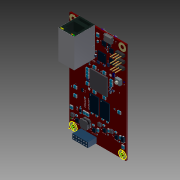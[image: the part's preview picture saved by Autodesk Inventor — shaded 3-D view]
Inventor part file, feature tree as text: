
AUTODESK INVENTOR PART (.ipt)
format: ipt  version: 2015 (Build 190159000, 159)  size: 6,993,920 bytes
history: native  units: in
note: dims shown in document units (in); Inventor stores cm internally (conversion verified against a paired STEP export)
features: imported_body x1163, extrude x1112, other x52, projected_geometry x25, sketch x3
ambient origin geometry x8: Origin, YZ Plane, XZ Plane, XY Plane, X Axis, Y Axis, Z Axis, Center Point
bodies: Body1 (feature_tree), Body2 (feature_tree), Body3 (feature_tree), Body4 (feature_tree), Body5 (feature_tree), Body6 (feature_tree), Body7 (feature_tree), Body8 (feature_tree), Body9 (feature_tree), Body10 (feature_tree), Body11 (feature_tree), Body12 (feature_tree), Body13 (feature_tree), Body14 (feature_tree), Body15 (feature_tree), Body16 (feature_tree), Body17 (feature_tree), Body18 (feature_tree), Body19 (feature_tree), Body20 (feature_tree), Body21 (feature_tree), Body22 (feature_tree), Body23 (feature_tree), Body24 (feature_tree), Body25 (feature_tree), Body26 (feature_tree), Body27 (feature_tree), Body28 (feature_tree), Body29 (feature_tree), Body30 (feature_tree), Body31 (feature_tree), Body32 (feature_tree), Body33 (feature_tree), Body34 (feature_tree), Body35 (feature_tree), Body36 (feature_tree), Body37 (feature_tree), Body38 (feature_tree), Body39 (feature_tree), Body40 (feature_tree), Body41 (feature_tree), Body42 (feature_tree), Body43 (feature_tree), Body44 (feature_tree), Body45 (feature_tree), Body46 (feature_tree), Body47 (feature_tree), Body48 (feature_tree), Body49 (feature_tree), Body50 (feature_tree), Body51 (feature_tree), Body52 (feature_tree), Body53 (feature_tree), Body54 (feature_tree), Body55 (feature_tree), Body56 (feature_tree), Body57 (feature_tree), Body58 (feature_tree), Body59 (feature_tree), Body60 (feature_tree), Body61 (feature_tree), Body62 (feature_tree), Body63 (feature_tree), Body64 (feature_tree), Body65 (feature_tree), Body66 (feature_tree), Body67 (feature_tree), Body68 (feature_tree), Body69 (feature_tree), Body70 (feature_tree), Body71 (feature_tree), Body72 (feature_tree), Body73 (feature_tree), Body74 (feature_tree), Body75 (feature_tree), Body76 (feature_tree), Body77 (feature_tree), Body78 (feature_tree), Body79 (feature_tree), Body80 (feature_tree), Body81 (feature_tree), Body82 (feature_tree), Body83 (feature_tree), Body84 (feature_tree), Body85 (feature_tree), Body86 (feature_tree), Body87 (feature_tree), Body88 (feature_tree), Body89 (feature_tree), Body90 (feature_tree), Body91 (feature_tree), Body92 (feature_tree), Body93 (feature_tree), Body94 (feature_tree), Body95 (feature_tree), Body96 (feature_tree), Body97 (feature_tree), Body98 (feature_tree), Body99 (feature_tree), Body100 (feature_tree), Body101 (feature_tree), Body102 (feature_tree), Body103 (feature_tree), Body104 (feature_tree), Body105 (feature_tree), Body106 (feature_tree), Body107 (feature_tree), Body108 (feature_tree), Body109 (feature_tree), Body110 (feature_tree), Body111 (feature_tree), Body112 (feature_tree), Body113 (feature_tree), Body114 (feature_tree), Body115 (feature_tree), Body116 (feature_tree), Body117 (feature_tree), Body118 (feature_tree), Body119 (feature_tree), Body120 (feature_tree), Body121 (feature_tree), Body122 (feature_tree), Body123 (feature_tree), Body124 (feature_tree), Body125 (feature_tree), Body126 (feature_tree), Body127 (feature_tree), Body128 (feature_tree), Body129 (feature_tree), Body130 (feature_tree), Body131 (feature_tree), Body132 (feature_tree), Body133 (feature_tree), Body134 (feature_tree), Body135 (feature_tree), Body136 (feature_tree), Body137 (feature_tree), Body138 (feature_tree), Body139 (feature_tree), Body140 (feature_tree), Body141 (feature_tree), Body142 (feature_tree), Body143 (feature_tree), Body144 (feature_tree), Body145 (feature_tree), Body146 (feature_tree), Body147 (feature_tree), Body148 (feature_tree), Body149 (feature_tree), Body150 (feature_tree), Body151 (feature_tree), Body152 (feature_tree), Body153 (feature_tree), Body154 (feature_tree), Body155 (feature_tree), Body156 (feature_tree), Body157 (feature_tree), Body158 (feature_tree), Body159 (feature_tree), Body160 (feature_tree), Body161 (feature_tree), Body162 (feature_tree), Body163 (feature_tree), Body164 (feature_tree), Body165 (feature_tree), Body166 (feature_tree), Body167 (feature_tree), Body168 (feature_tree), Body169 (feature_tree), Body170 (feature_tree), Body171 (feature_tree), Body172 (feature_tree), Body173 (feature_tree), Body174 (feature_tree), Body175 (feature_tree), Body176 (feature_tree), Body177 (feature_tree), Body178 (feature_tree), Body179 (feature_tree), Body180 (feature_tree), Body181 (feature_tree), Body182 (feature_tree), Body183 (feature_tree), Body184 (feature_tree), Body185 (feature_tree), Body186 (feature_tree), Body187 (feature_tree), Body188 (feature_tree), Body189 (feature_tree), Body190 (feature_tree), Body191 (feature_tree), Body192 (feature_tree), Body193 (feature_tree), Body194 (feature_tree), Body195 (feature_tree), Body196 (feature_tree), Body197 (feature_tree), Body198 (feature_tree), Body199 (feature_tree), Body200 (feature_tree), Body201 (feature_tree), Body202 (feature_tree), Body203 (feature_tree), Body204 (feature_tree), Body205 (feature_tree), Body206 (feature_tree), Body207 (feature_tree), Body208 (feature_tree), Body209 (feature_tree), Body210 (feature_tree), Body211 (feature_tree), Body212 (feature_tree), Body213 (feature_tree), Body214 (feature_tree), Body215 (feature_tree), Body216 (feature_tree), Body217 (feature_tree), Body218 (feature_tree), Body219 (feature_tree), Body220 (feature_tree), Body221 (feature_tree), Body222 (feature_tree), Body223 (feature_tree), Body224 (feature_tree), Body225 (feature_tree), Body226 (feature_tree), Body227 (feature_tree), Body228 (feature_tree), Body229 (feature_tree), Body230 (feature_tree), Body231 (feature_tree), Body232 (feature_tree), Body233 (feature_tree), Body234 (feature_tree), Body235 (feature_tree), Body236 (feature_tree), Body237 (feature_tree), Body238 (feature_tree), Body239 (feature_tree), Body240 (feature_tree), Body241 (feature_tree), Body242 (feature_tree), Body243 (feature_tree), Body244 (feature_tree), Body245 (feature_tree), Body246 (feature_tree), Body247 (feature_tree), Body248 (feature_tree), Body249 (feature_tree), Body250 (feature_tree), Body251 (feature_tree), Body252 (feature_tree), Body253 (feature_tree), Body254 (feature_tree), Body255 (feature_tree), Body256 (feature_tree), Body257 (feature_tree), Body258 (feature_tree), Body259 (feature_tree), Body260 (feature_tree), Body261 (feature_tree), Body262 (feature_tree), Body263 (feature_tree), Body264 (feature_tree), Body265 (feature_tree), Body266 (feature_tree), Body267 (feature_tree), Body268 (feature_tree), Body269 (feature_tree), Body270 (feature_tree), Body271 (feature_tree), Body272 (feature_tree), Body273 (feature_tree), Body274 (feature_tree), Body275 (feature_tree), Body276 (feature_tree), Body277 (feature_tree), Body278 (feature_tree), Body279 (feature_tree), Body280 (feature_tree), Body281 (feature_tree), Body282 (feature_tree), Body283 (feature_tree), Body284 (feature_tree), Body285 (feature_tree), Body286 (feature_tree), Body287 (feature_tree), Body288 (feature_tree), Body289 (feature_tree), Body290 (feature_tree), Body291 (feature_tree), Body292 (feature_tree), Body293 (feature_tree), Body294 (feature_tree), Body295 (feature_tree), Body296 (feature_tree), Body297 (feature_tree), Body298 (feature_tree), Body299 (feature_tree), Body300 (feature_tree), Body301 (feature_tree), Body302 (feature_tree), Body303 (feature_tree), Body304 (feature_tree), Body305 (feature_tree), Body306 (feature_tree), Body307 (feature_tree), Body308 (feature_tree), Body309 (feature_tree), Body310 (feature_tree), Body311 (feature_tree), Body312 (feature_tree), Body313 (feature_tree), Body314 (feature_tree), Body315 (feature_tree), Body316 (feature_tree), Body317 (feature_tree), Body318 (feature_tree), Body319 (feature_tree), Body320 (feature_tree), Body321 (feature_tree), Body322 (feature_tree), Body323 (feature_tree), Body324 (feature_tree), Body325 (feature_tree), Body326 (feature_tree), Body327 (feature_tree), Body328 (feature_tree), Body329 (feature_tree), Body330 (feature_tree), Body331 (feature_tree), Body332 (feature_tree), Body333 (feature_tree), Body334 (feature_tree), Body335 (feature_tree), Body336 (feature_tree), Body337 (feature_tree), Body338 (feature_tree), Body339 (feature_tree), Body340 (feature_tree), Body341 (feature_tree), Body342 (feature_tree), Body343 (feature_tree), Body344 (feature_tree), Body345 (feature_tree), Body346 (feature_tree), Body347 (feature_tree), Body348 (feature_tree), Body349 (feature_tree), Body350 (feature_tree), Body351 (feature_tree), Body352 (feature_tree), Body353 (feature_tree), Body354 (feature_tree), Body355 (feature_tree), Body356 (feature_tree), Body357 (feature_tree), Body358 (feature_tree), Body359 (feature_tree), Body360 (feature_tree), Body361 (feature_tree), Body362 (feature_tree), Body363 (feature_tree), Body364 (feature_tree), Body365 (feature_tree), Body366 (feature_tree), Body367 (feature_tree), Body368 (feature_tree), Body369 (feature_tree), Body370 (feature_tree), Body371 (feature_tree), Body372 (feature_tree), Body373 (feature_tree), Body374 (feature_tree), Body375 (feature_tree), Body376 (feature_tree), Body377 (feature_tree), Body378 (feature_tree), Body379 (feature_tree), Body380 (feature_tree), Body381 (feature_tree), Body382 (feature_tree), Body383 (feature_tree), Body384 (feature_tree), Body385 (feature_tree), Body386 (feature_tree), Body387 (feature_tree), Body388 (feature_tree), Body389 (feature_tree), Body390 (feature_tree), Body391 (feature_tree), Body392 (feature_tree), Body393 (feature_tree), Body394 (feature_tree), Body395 (feature_tree), Body396 (feature_tree), Body397 (feature_tree), Body398 (feature_tree), Body399 (feature_tree), Body400 (feature_tree), Body401 (feature_tree), Body402 (feature_tree), Body403 (feature_tree), Body404 (feature_tree), Body405 (feature_tree), Body406 (feature_tree), Body407 (feature_tree), Body408 (feature_tree), Body409 (feature_tree), Body410 (feature_tree), Body411 (feature_tree), Body412 (feature_tree), Body413 (feature_tree), Body414 (feature_tree), Body415 (feature_tree), Body416 (feature_tree), Body417 (feature_tree), Body418 (feature_tree), Body419 (feature_tree), Body420 (feature_tree), Body421 (feature_tree), Body422 (feature_tree), Body423 (feature_tree), Body424 (feature_tree), Body425 (feature_tree), Body426 (feature_tree), Body427 (feature_tree), Body428 (feature_tree), Body429 (feature_tree), Body430 (feature_tree), Body431 (feature_tree), Body432 (feature_tree), Body433 (feature_tree), Body434 (feature_tree), Body435 (feature_tree), Body436 (feature_tree), Body437 (feature_tree), Body438 (feature_tree), Body439 (feature_tree), Body440 (feature_tree), Body441 (feature_tree), Body442 (feature_tree), Body443 (feature_tree), Body444 (feature_tree), Body445 (feature_tree), Body446 (feature_tree), Body447 (feature_tree), Body448 (feature_tree), Body449 (feature_tree), Body450 (feature_tree), Body451 (feature_tree), Body452 (feature_tree), Body453 (feature_tree), Body454 (feature_tree), Body455 (feature_tree), Body456 (feature_tree), Body457 (feature_tree), Body458 (feature_tree), Body459 (feature_tree), Body460 (feature_tree), Body461 (feature_tree), Body462 (feature_tree), Body463 (feature_tree), Body464 (feature_tree), Body465 (feature_tree), Body466 (feature_tree), Body467 (feature_tree), Body468 (feature_tree), Body469 (feature_tree), Body470 (feature_tree), Body471 (feature_tree), Body472 (feature_tree), Body473 (feature_tree), Body474 (feature_tree), Body475 (feature_tree), Body476 (feature_tree), Body477 (feature_tree), Body478 (feature_tree), Body479 (feature_tree), Body480 (feature_tree), Body481 (feature_tree), Body482 (feature_tree), Body483 (feature_tree), Body484 (feature_tree), Body485 (feature_tree), Body486 (feature_tree), Body487 (feature_tree), Body488 (feature_tree), Body489 (feature_tree), Body490 (feature_tree), Body491 (feature_tree), Body492 (feature_tree), Body493 (feature_tree), Body494 (feature_tree), Body495 (feature_tree), Body496 (feature_tree), Body497 (feature_tree), Body498 (feature_tree), Body499 (feature_tree), Body500 (feature_tree), Body501 (feature_tree), Body502 (feature_tree), Body503 (feature_tree), Body504 (feature_tree), Body505 (feature_tree), Body506 (feature_tree), Body507 (feature_tree), Body508 (feature_tree), Body509 (feature_tree), Body510 (feature_tree), Body511 (feature_tree), Body512 (feature_tree), Body513 (feature_tree), Body514 (feature_tree), Body515 (feature_tree), Body516 (feature_tree), Body517 (feature_tree), Body518 (feature_tree), Body519 (feature_tree), Body520 (feature_tree), Body521 (feature_tree), Body522 (feature_tree), Body523 (feature_tree), Body524 (feature_tree), Body525 (feature_tree), Body526 (feature_tree), Body527 (feature_tree), Body528 (feature_tree), Body529 (feature_tree), Body530 (feature_tree), Body531 (feature_tree), Body532 (feature_tree), Body533 (feature_tree), Body534 (feature_tree), Body535 (feature_tree), Body536 (feature_tree), Body537 (feature_tree), Body538 (feature_tree), Body539 (feature_tree), Body540 (feature_tree), Body541 (feature_tree), Body542 (feature_tree), Body543 (feature_tree), Body544 (feature_tree), Body545 (feature_tree), Body546 (feature_tree), Body547 (feature_tree), Body548 (feature_tree), Body549 (feature_tree), Body550 (feature_tree), Body551 (feature_tree), Body552 (feature_tree), Body553 (feature_tree), Body554 (feature_tree), Body555 (feature_tree), Body556 (feature_tree), Body557 (feature_tree), Body558 (feature_tree), Body559 (feature_tree), Body560 (feature_tree), Body561 (feature_tree), Body562 (feature_tree), Body563 (feature_tree), Body564 (feature_tree), Body565 (feature_tree), Body566 (feature_tree), Body567 (feature_tree), Body568 (feature_tree), Body569 (feature_tree), Body570 (feature_tree), Body571 (feature_tree), Body572 (feature_tree), Body573 (feature_tree), Body574 (feature_tree), Body575 (feature_tree), Body576 (feature_tree), Body577 (feature_tree), Body578 (feature_tree), Body579 (feature_tree), Body580 (feature_tree), Body581 (feature_tree), Body582 (feature_tree), Body583 (feature_tree), Body584 (feature_tree), Body585 (feature_tree), Body586 (feature_tree), Body587 (feature_tree), Body588 (feature_tree), Body589 (feature_tree), Body590 (feature_tree), Body591 (feature_tree), Body592 (feature_tree), Body593 (feature_tree), Body594 (feature_tree), Body595 (feature_tree), Body596 (feature_tree), Body597 (feature_tree), Body598 (feature_tree), Body599 (feature_tree), Body600 (feature_tree), Body601 (feature_tree), Body602 (feature_tree), Body603 (feature_tree), Body604 (feature_tree), Body605 (feature_tree), Body606 (feature_tree), Body607 (feature_tree), Body608 (feature_tree), Body609 (feature_tree), Body610 (feature_tree), Body611 (feature_tree), Body612 (feature_tree), Body613 (feature_tree), Body614 (feature_tree), Body615 (feature_tree), Body616 (feature_tree), Body617 (feature_tree), Body618 (feature_tree), Body619 (feature_tree), Body620 (feature_tree), Body621 (feature_tree), Body622 (feature_tree), Body623 (feature_tree), Body624 (feature_tree), Body625 (feature_tree), Body626 (feature_tree), Body627 (feature_tree), Body628 (feature_tree), Body629 (feature_tree), Body630 (feature_tree), Body631 (feature_tree), Body632 (feature_tree), Body633 (feature_tree), Body634 (feature_tree), Body635 (feature_tree), Body636 (feature_tree), Body637 (feature_tree), Body638 (feature_tree), Body639 (feature_tree), Body640 (feature_tree), Body641 (feature_tree), Body642 (feature_tree), Body643 (feature_tree), Body644 (feature_tree), Body645 (feature_tree), Body646 (feature_tree), Body647 (feature_tree), Body648 (feature_tree), Body649 (feature_tree), Body650 (feature_tree), Body651 (feature_tree), Body652 (feature_tree), Body653 (feature_tree), Body654 (feature_tree), Body655 (feature_tree), Body656 (feature_tree), Body657 (feature_tree), Body658 (feature_tree), Body659 (feature_tree), Body660 (feature_tree), Body661 (feature_tree), Body662 (feature_tree), Body663 (feature_tree), Body664 (feature_tree), Body665 (feature_tree), Body666 (feature_tree), Body667 (feature_tree), Body668 (feature_tree), Body669 (feature_tree), Body670 (feature_tree), Body671 (feature_tree), Body672 (feature_tree), Body673 (feature_tree), Body674 (feature_tree), Body675 (feature_tree), Body676 (feature_tree), Body677 (feature_tree), Body678 (feature_tree), Body679 (feature_tree), Body680 (feature_tree), Body681 (feature_tree), Body682 (feature_tree), Body683 (feature_tree), Body684 (feature_tree), Body685 (feature_tree), Body686 (feature_tree), Body687 (feature_tree), Body688 (feature_tree), Body689 (feature_tree), Body690 (feature_tree), Body691 (feature_tree), Body692 (feature_tree), Body693 (feature_tree), Body694 (feature_tree), Body695 (feature_tree), Body696 (feature_tree), Body697 (feature_tree), Body698 (feature_tree), Body699 (feature_tree), Body700 (feature_tree), Body701 (feature_tree), Body702 (feature_tree), Body703 (feature_tree), Body704 (feature_tree), Body705 (feature_tree), Body706 (feature_tree), Body707 (feature_tree), Body708 (feature_tree), Body709 (feature_tree), Body710 (feature_tree), Body711 (feature_tree), Body712 (feature_tree), Body713 (feature_tree), Body714 (feature_tree), Body715 (feature_tree), Body716 (feature_tree), Body717 (feature_tree), Body718 (feature_tree), Body719 (feature_tree), Body720 (feature_tree), Body721 (feature_tree), Body722 (feature_tree), Body723 (feature_tree), Body724 (feature_tree), Body725 (feature_tree), Body726 (feature_tree), Body727 (feature_tree), Body728 (feature_tree), Body729 (feature_tree), Body730 (feature_tree), Body731 (feature_tree), Body732 (feature_tree), Body733 (feature_tree), Body734 (feature_tree), Body735 (feature_tree), Body736 (feature_tree), Body737 (feature_tree), Body738 (feature_tree), Body739 (feature_tree), Body740 (feature_tree), Body741 (feature_tree), Body742 (feature_tree), Body743 (feature_tree), Body744 (feature_tree), Body745 (feature_tree), Body746 (feature_tree), Body747 (feature_tree), Body748 (feature_tree), Body749 (feature_tree), Body750 (feature_tree), Body751 (feature_tree), Body752 (feature_tree), Body753 (feature_tree), Body754 (feature_tree), Body755 (feature_tree), Body756 (feature_tree), Body757 (feature_tree), Body758 (feature_tree), Body759 (feature_tree), Body760 (feature_tree), Body761 (feature_tree), Body762 (feature_tree), Body763 (feature_tree), Body764 (feature_tree), Body765 (feature_tree), Body766 (feature_tree), Body767 (feature_tree), Body768 (feature_tree), Body769 (feature_tree), Body770 (feature_tree), Body771 (feature_tree), Body772 (feature_tree), Body773 (feature_tree), Body774 (feature_tree), Body775 (feature_tree), Body776 (feature_tree), Body777 (feature_tree), Body778 (feature_tree), Body779 (feature_tree), Body780 (feature_tree), Body781 (feature_tree), Body782 (feature_tree), Body783 (feature_tree), Body784 (feature_tree), Body785 (feature_tree), Body786 (feature_tree), Body787 (feature_tree), Body788 (feature_tree), Body789 (feature_tree), Body790 (feature_tree), Body791 (feature_tree), Body792 (feature_tree), Body793 (feature_tree), Body794 (feature_tree), Body795 (feature_tree), Body796 (feature_tree), Body797 (feature_tree), Body798 (feature_tree), Body799 (feature_tree), Body800 (feature_tree), Body801 (feature_tree), Body802 (feature_tree), Body803 (feature_tree), Body804 (feature_tree), Body805 (feature_tree), Body806 (feature_tree), Body807 (feature_tree), Body808 (feature_tree), Body809 (feature_tree), Body810 (feature_tree), Body811 (feature_tree), Body812 (feature_tree), Body813 (feature_tree), Body814 (feature_tree), Body815 (feature_tree), Body816 (feature_tree), Body817 (feature_tree), Body818 (feature_tree), Body819 (feature_tree), Body820 (feature_tree), Body821 (feature_tree), Body822 (feature_tree), Body823 (feature_tree), Body824 (feature_tree), Body825 (feature_tree), Body826 (feature_tree), Body827 (feature_tree), Body828 (feature_tree), Body829 (feature_tree), Body830 (feature_tree), Body831 (feature_tree), Body832 (feature_tree), Body833 (feature_tree), Body834 (feature_tree), Body835 (feature_tree), Body836 (feature_tree), Body837 (feature_tree), Body838 (feature_tree), Body839 (feature_tree), Body840 (feature_tree), Body841 (feature_tree), Body842 (feature_tree), Body843 (feature_tree), Body844 (feature_tree), Body845 (feature_tree), Body846 (feature_tree), Body847 (feature_tree), Body848 (feature_tree), Body849 (feature_tree), Body850 (feature_tree), Body851 (feature_tree), Body852 (feature_tree), Body853 (feature_tree), Body854 (feature_tree), Body855 (feature_tree), Body856 (feature_tree), Body857 (feature_tree), Body858 (feature_tree), Body859 (feature_tree), Body860 (feature_tree), Body861 (feature_tree), Body862 (feature_tree), Body863 (feature_tree), Body864 (feature_tree), Body865 (feature_tree), Body866 (feature_tree), Body867 (feature_tree), Body868 (feature_tree), Body869 (feature_tree), Body870 (feature_tree), Body871 (feature_tree), Body872 (feature_tree), Body873 (feature_tree), Body874 (feature_tree), Body875 (feature_tree), Body876 (feature_tree), Body877 (feature_tree), Body878 (feature_tree), Body879 (feature_tree), Body880 (feature_tree), Body881 (feature_tree), Body882 (feature_tree), Body883 (feature_tree), Body884 (feature_tree), Body885 (feature_tree), Body886 (feature_tree), Body887 (feature_tree), Body888 (feature_tree), Body889 (feature_tree), Body890 (feature_tree), Body891 (feature_tree), Body892 (feature_tree), Body893 (feature_tree), Body894 (feature_tree), Body895 (feature_tree), Body896 (feature_tree), Body897 (feature_tree), Body898 (feature_tree), Body899 (feature_tree), Body900 (feature_tree), Body901 (feature_tree), Body902 (feature_tree), Body903 (feature_tree), Body904 (feature_tree), Body905 (feature_tree), Body906 (feature_tree), Body907 (feature_tree), Body908 (feature_tree), Body909 (feature_tree), Body910 (feature_tree), Body911 (feature_tree), Body912 (feature_tree), Body913 (feature_tree), Body914 (feature_tree), Body915 (feature_tree), Body916 (feature_tree), Body917 (feature_tree), Body918 (feature_tree), Body919 (feature_tree), Body920 (feature_tree), Body921 (feature_tree), Body922 (feature_tree), Body923 (feature_tree), Body924 (feature_tree), Body925 (feature_tree), Body926 (feature_tree), Body927 (feature_tree), Body928 (feature_tree), Body929 (feature_tree), Body930 (feature_tree), Body931 (feature_tree), Body932 (feature_tree), Body933 (feature_tree), Body934 (feature_tree), Body935 (feature_tree), Body936 (feature_tree), Body937 (feature_tree), Body938 (feature_tree), Body939 (feature_tree), Body940 (feature_tree), Body941 (feature_tree), Body942 (feature_tree), Body943 (feature_tree), Body944 (feature_tree), Body945 (feature_tree), Body946 (feature_tree), Body947 (feature_tree), Body948 (feature_tree), Body949 (feature_tree), Body950 (feature_tree), Body951 (feature_tree), Body952 (feature_tree), Body953 (feature_tree), Body954 (feature_tree), Body955 (feature_tree), Body956 (feature_tree), Body957 (feature_tree), Body958 (feature_tree), Body959 (feature_tree), Body960 (feature_tree), Body961 (feature_tree), Body962 (feature_tree), Body963 (feature_tree), Body964 (feature_tree), Body965 (feature_tree), Body966 (feature_tree), Body967 (feature_tree), Body968 (feature_tree), Body969 (feature_tree), Body970 (feature_tree), Body971 (feature_tree), Body972 (feature_tree), Body973 (feature_tree), Body974 (feature_tree), Body975 (feature_tree), Body976 (feature_tree), Body977 (feature_tree), Body978 (feature_tree), Body979 (feature_tree), Body980 (feature_tree), Body981 (feature_tree), Body982 (feature_tree), Body983 (feature_tree), Body984 (feature_tree), Body985 (feature_tree), Body986 (feature_tree), Body987 (feature_tree), Body988 (feature_tree), Body989 (feature_tree), Body990 (feature_tree), Body991 (feature_tree), Body992 (feature_tree), Body993 (feature_tree), Body994 (feature_tree), Body995 (feature_tree), Body996 (feature_tree), Body997 (feature_tree), Body998 (feature_tree), Body999 (feature_tree), Body1000 (feature_tree), Body1001 (feature_tree), Body1002 (feature_tree), Body1003 (feature_tree), Body1004 (feature_tree), Body1005 (feature_tree), Body1006 (feature_tree), Body1007 (feature_tree), Body1008 (feature_tree), Body1009 (feature_tree), Body1010 (feature_tree), Body1011 (feature_tree), Body1012 (feature_tree), Body1013 (feature_tree), Body1014 (feature_tree), Body1015 (feature_tree), Body1016 (feature_tree), Body1017 (feature_tree), Body1018 (feature_tree), Body1019 (feature_tree), Body1020 (feature_tree), Body1021 (feature_tree), Body1022 (feature_tree), Body1023 (feature_tree), Body1024 (feature_tree), Body1025 (feature_tree), Body1026 (feature_tree), Body1027 (feature_tree), Body1028 (feature_tree), Body1029 (feature_tree), Body1030 (feature_tree), Body1031 (feature_tree), Body1032 (feature_tree), Body1033 (feature_tree), Body1034 (feature_tree), Body1035 (feature_tree), Body1036 (feature_tree), Body1037 (feature_tree), Body1038 (feature_tree), Body1039 (feature_tree), Body1040 (feature_tree), Body1041 (feature_tree), Body1042 (feature_tree), Body1043 (feature_tree), Body1044 (feature_tree), Body1045 (feature_tree), Body1046 (feature_tree), Body1047 (feature_tree), Body1048 (feature_tree), Body1049 (feature_tree), Body1050 (feature_tree), Body1051 (feature_tree), Body1052 (feature_tree), Body1053 (feature_tree), Body1054 (feature_tree), Body1055 (feature_tree), Body1056 (feature_tree), Body1057 (feature_tree), Body1058 (feature_tree), Body1059 (feature_tree), Body1060 (feature_tree), Body1061 (feature_tree), Body1062 (feature_tree), Body1063 (feature_tree), Body1064 (feature_tree), Body1065 (feature_tree), Body1066 (feature_tree), Body1067 (feature_tree), Body1068 (feature_tree), Body1069 (feature_tree), Body1070 (feature_tree), Body1071 (feature_tree), Body1072 (feature_tree), Body1073 (feature_tree), Body1074 (feature_tree), Body1075 (feature_tree), Body1076 (feature_tree), Body1077 (feature_tree), Body1078 (feature_tree), Body1079 (feature_tree), Body1080 (feature_tree), Body1081 (feature_tree), Body1082 (feature_tree), Body1083 (feature_tree), Body1084 (feature_tree), Body1085 (feature_tree), Body1086 (feature_tree), Body1087 (feature_tree), Body1088 (feature_tree), Body1089 (feature_tree), Body1090 (feature_tree), Body1091 (feature_tree), Body1092 (feature_tree), Body1093 (feature_tree), Body1094 (feature_tree), Body1095 (feature_tree), Body1096 (feature_tree), Body1097 (feature_tree), Body1098 (feature_tree), Body1099 (feature_tree), Body1100 (feature_tree), Body1101 (feature_tree), Body1102 (feature_tree), Body1103 (feature_tree), Body1104 (feature_tree), Body1105 (feature_tree), Body1106 (feature_tree), Body1107 (feature_tree), Body1108 (feature_tree), Body1109 (feature_tree), Body1110 (feature_tree), Body1111 (feature_tree), Body1112 (feature_tree), Body1113 (feature_tree), Body1114 (feature_tree), Body1115 (feature_tree), Body1116 (feature_tree), Body1117 (feature_tree), Body1118 (feature_tree), Body1119 (feature_tree), Body1120 (feature_tree), Body1121 (feature_tree), Body1122 (feature_tree), Body1123 (feature_tree), Body1124 (feature_tree), Body1125 (feature_tree), Body1126 (feature_tree), Body1127 (feature_tree), Body1128 (feature_tree), Body1129 (feature_tree), Body1130 (feature_tree), Body1131 (feature_tree), Body1132 (feature_tree), Body1133 (feature_tree), Body1134 (feature_tree), Body1135 (feature_tree), Body1136 (feature_tree), Body1137 (feature_tree), Body1138 (feature_tree), Body1139 (feature_tree), Body1140 (feature_tree), Body1141 (feature_tree), Body1142 (feature_tree), Body1143 (feature_tree), Body1144 (feature_tree), Body1145 (feature_tree), Body1146 (feature_tree), Body1147 (feature_tree), Body1148 (feature_tree), Body1149 (feature_tree), Body1150 (feature_tree), Body1151 (feature_tree), Body1152 (feature_tree), Body1153 (feature_tree), Body1154 (feature_tree), Body1155 (feature_tree), Body1156 (feature_tree), Body1157 (feature_tree), Body1158 (feature_tree), Body1159 (feature_tree), Body1160 (feature_tree), Body1161 (feature_tree), Body1162 (feature_tree), Body1163 (feature_tree)
feature tree (2355):
  other  "Board"
  other  "Repaired Geometry1"
  sketch  "Sketch1"  dims[d3=0.3009in d4=0.0005in]
  sketch  "Sketch2"  dims[d5=0.0653in d6=0.0653in d7=0.0653in d8=0.0653in d9=0.0653in d10=0.0653in d11=0.0653in d12=0.0653in d13=0.0098in d14=0.0098in d15=1.1299in d16=1.1299in d17=1.7402in d18=0.0404in]
  extrude  "Extruded"  Depth=0.3009in
  extrude  "Extruded_1"  Depth=0.0653in
  extrude  "Extruded_2"  Depth=0.0653in
  extrude  "Extruded_3"  Depth=0.0653in
  extrude  "Extruded_4"  Depth=0.0653in
  extrude  "Extruded_5"  Depth=0.0653in
  extrude  "Extruded_6"  Depth=0.0653in
  extrude  "Extruded_7"  Depth=0.0653in
  extrude  "Extruded_8"  Depth=0.0404in
  extrude  "Extruded_9"  Depth=0.0404in
  extrude  "Extruded_10"  Depth=1.1299in
  extrude  "Extruded_11"  Depth=1.1299in
  extrude  "Extruded_12"  Depth=1.7402in
  extrude  "Extruded_13"  Depth=0.0404in
  extrude  "Extruded_14"  [1 undecoded]
  extrude  "Extruded_15"  [1 undecoded]
  extrude  "Extruded_16"  [1 undecoded]
  extrude  "Extruded_17"  [1 undecoded]
  extrude  "Extruded_18"  [1 undecoded]
  extrude  "Extruded_19"  [1 undecoded]
  extrude  "Extruded_20"  [1 undecoded]
  extrude  "Extruded_21"  [1 undecoded]
  extrude  "Extruded_22"  [1 undecoded]
  extrude  "Extruded_23"  [1 undecoded]
  extrude  "Extruded_24"  [1 undecoded]
  extrude  "Extruded_25"  [1 undecoded]
  extrude  "Extruded_26"  [1 undecoded]
  extrude  "Extruded_27"  [1 undecoded]
  other  "Cylinder"
  other  "Cylinder_1"
  other  "Cylinder_2"
  other  "Cylinder_3"
  extrude  "Extruded_28"  [1 undecoded]
  extrude  "Extruded_29"  [1 undecoded]
  other  "Cylinder_4"
  extrude  "Extruded_30"  [1 undecoded]
  other  "Cylinder_5"
  extrude  "Extruded_31"  [1 undecoded]
  other  "Cylinder_6"
  other  "Cylinder_7"
  extrude  "Extruded_32"  [1 undecoded]
  extrude  "Extruded_33"  [1 undecoded]
  extrude  "Extruded_34"  [1 undecoded]
  extrude  "Extruded_35"  [1 undecoded]
  extrude  "Extruded_36"  [1 undecoded]
  extrude  "Extruded_37"  [1 undecoded]
  extrude  "Extruded_38"  [1 undecoded]
  extrude  "Extruded_39"  [1 undecoded]
  extrude  "Extruded_40"  [1 undecoded]
  extrude  "Extruded_41"  [1 undecoded]
  extrude  "Extruded_42"  [1 undecoded]
  extrude  "Extruded_43"  [1 undecoded]
  extrude  "Extruded_44"  [1 undecoded]
  extrude  "Extruded_45"  [1 undecoded]
  extrude  "Extruded_46"  [1 undecoded]
  extrude  "Extruded_47"  [1 undecoded]
  extrude  "Extruded_48"  [1 undecoded]
  extrude  "Extruded_49"  [1 undecoded]
  extrude  "Extruded_50"  [1 undecoded]
  extrude  "Extruded_51"  [1 undecoded]
  extrude  "Extruded_52"  [1 undecoded]
  extrude  "Extruded_53"  [1 undecoded]
  extrude  "Extruded_54"  [1 undecoded]
  extrude  "Extruded_55"  [1 undecoded]
  extrude  "Extruded_56"  [1 undecoded]
  extrude  "Extruded_57"  [1 undecoded]
  extrude  "Extruded_58"  [1 undecoded]
  extrude  "Extruded_59"  [1 undecoded]
  extrude  "Extruded_60"  [1 undecoded]
  extrude  "Extruded_61"  [1 undecoded]
  extrude  "Extruded_62"  [1 undecoded]
  extrude  "Extruded_63"  [1 undecoded]
  extrude  "Extruded_64"  [1 undecoded]
  extrude  "Extruded_65"  [1 undecoded]
  extrude  "Extruded_66"  [1 undecoded]
  extrude  "Extruded_67"  [1 undecoded]
  extrude  "Extruded_68"  [1 undecoded]
  extrude  "Extruded_69"  [1 undecoded]
  extrude  "Extruded_70"  [1 undecoded]
  extrude  "Extruded_71"  [1 undecoded]
  extrude  "Extruded_72"  [1 undecoded]
  extrude  "Extruded_73"  [1 undecoded]
  extrude  "Extruded_74"  [1 undecoded]
  extrude  "Extruded_75"  [1 undecoded]
  extrude  "Extruded_76"  [1 undecoded]
  extrude  "Extruded_77"  [1 undecoded]
  extrude  "Extruded_78"  [1 undecoded]
  extrude  "Extruded_79"  [1 undecoded]
  extrude  "Extruded_80"  [1 undecoded]
  extrude  "Extruded_81"  [1 undecoded]
  extrude  "Extruded_82"  [1 undecoded]
  extrude  "Extruded_83"  [1 undecoded]
  extrude  "Extruded_84"  [1 undecoded]
  extrude  "Extruded_85"  [1 undecoded]
  extrude  "Extruded_86"  [1 undecoded]
  extrude  "Extruded_87"  [1 undecoded]
  extrude  "Extruded_88"  [1 undecoded]
  extrude  "Extruded_89"  [1 undecoded]
  extrude  "Extruded_90"  [1 undecoded]
  extrude  "Extruded_91"  [1 undecoded]
  extrude  "Extruded_92"  [1 undecoded]
  extrude  "Extruded_93"  [1 undecoded]
  extrude  "Extruded_94"  [1 undecoded]
  extrude  "Extruded_95"  [1 undecoded]
  extrude  "Extruded_96"  [1 undecoded]
  extrude  "Extruded_97"  [1 undecoded]
  extrude  "Extruded_98"  [1 undecoded]
  extrude  "Extruded_99"  [1 undecoded]
  extrude  "Extruded_100"  [1 undecoded]
  extrude  "Extruded_101"  [1 undecoded]
  extrude  "Extruded_102"  [1 undecoded]
  extrude  "Extruded_103"  [1 undecoded]
  extrude  "Extruded_104"  [1 undecoded]
  extrude  "Extruded_105"  [1 undecoded]
  extrude  "Extruded_106"  [1 undecoded]
  extrude  "Extruded_107"  [1 undecoded]
  extrude  "Extruded_108"  [1 undecoded]
  extrude  "Extruded_109"  [1 undecoded]
  extrude  "Extruded_110"  [1 undecoded]
  extrude  "Extruded_111"  [1 undecoded]
  extrude  "Extruded_112"  [1 undecoded]
  extrude  "Extruded_113"  [1 undecoded]
  extrude  "Extruded_114"  [1 undecoded]
  extrude  "Extruded_115"  [1 undecoded]
  extrude  "Extruded_116"  [1 undecoded]
  extrude  "Extruded_117"  [1 undecoded]
  extrude  "Extruded_118"  [1 undecoded]
  extrude  "Extruded_119"  [1 undecoded]
  extrude  "Extruded_120"  [1 undecoded]
  extrude  "Extruded_121"  [1 undecoded]
  extrude  "Extruded_122"  [1 undecoded]
  extrude  "Extruded_123"  [1 undecoded]
  extrude  "Extruded_124"  [1 undecoded]
  extrude  "Extruded_125"  [1 undecoded]
  extrude  "Extruded_126"  [1 undecoded]
  extrude  "Extruded_127"  [1 undecoded]
  extrude  "Extruded_128"  [1 undecoded]
  extrude  "Extruded_129"  [1 undecoded]
  extrude  "Extruded_130"  [1 undecoded]
  extrude  "Extruded_131"  [1 undecoded]
  extrude  "Extruded_132"  [1 undecoded]
  extrude  "Extruded_133"  [1 undecoded]
  extrude  "Extruded_134"  [1 undecoded]
  extrude  "Extruded_135"  [1 undecoded]
  extrude  "Extruded_136"  [1 undecoded]
  extrude  "Extruded_137"  [1 undecoded]
  extrude  "Extruded_138"  [1 undecoded]
  extrude  "Extruded_139"  [1 undecoded]
  extrude  "Extruded_140"  [1 undecoded]
  extrude  "Extruded_141"  [1 undecoded]
  extrude  "Extruded_142"  [1 undecoded]
  extrude  "Extruded_143"  [1 undecoded]
  extrude  "Extruded_144"  [1 undecoded]
  extrude  "Extruded_145"  [1 undecoded]
  extrude  "Extruded_146"  [1 undecoded]
  extrude  "Extruded_147"  [1 undecoded]
  extrude  "Extruded_148"  [1 undecoded]
  extrude  "Extruded_149"  [1 undecoded]
  extrude  "Extruded_150"  [1 undecoded]
  extrude  "Extruded_151"  [1 undecoded]
  extrude  "Extruded_152"  [1 undecoded]
  extrude  "Extruded_153"  [1 undecoded]
  extrude  "Extruded_154"  [1 undecoded]
  extrude  "Extruded_155"  [1 undecoded]
  extrude  "Extruded_156"  [1 undecoded]
  extrude  "Extruded_157"  [1 undecoded]
  extrude  "Extruded_158"  [1 undecoded]
  extrude  "Extruded_159"  [1 undecoded]
  extrude  "Extruded_160"  [1 undecoded]
  extrude  "Extruded_161"  [1 undecoded]
  extrude  "Extruded_162"  [1 undecoded]
  extrude  "Extruded_163"  [1 undecoded]
  extrude  "Extruded_164"  [1 undecoded]
  extrude  "Extruded_165"  [1 undecoded]
  extrude  "Extruded_166"  [1 undecoded]
  extrude  "Extruded_167"  [1 undecoded]
  extrude  "Extruded_168"  [1 undecoded]
  extrude  "Extruded_169"  [1 undecoded]
  extrude  "Extruded_170"  [1 undecoded]
  extrude  "Extruded_171"  [1 undecoded]
  extrude  "Extruded_172"  [1 undecoded]
  extrude  "Extruded_173"  [1 undecoded]
  extrude  "Extruded_174"  [1 undecoded]
  extrude  "Extruded_175"  [1 undecoded]
  extrude  "Extruded_176"  [1 undecoded]
  extrude  "Extruded_177"  [1 undecoded]
  extrude  "Extruded_178"  [1 undecoded]
  extrude  "Extruded_179"  [1 undecoded]
  extrude  "Extruded_180"  [1 undecoded]
  extrude  "Extruded_181"  [1 undecoded]
  extrude  "Extruded_182"  [1 undecoded]
  extrude  "Extruded_183"  [1 undecoded]
  extrude  "Extruded_184"  [1 undecoded]
  extrude  "Extruded_185"  [1 undecoded]
  extrude  "Extruded_186"  [1 undecoded]
  extrude  "Extruded_187"  [1 undecoded]
  extrude  "Extruded_188"  [1 undecoded]
  extrude  "Extruded_189"  [1 undecoded]
  extrude  "Extruded_190"  [1 undecoded]
  extrude  "Extruded_191"  [1 undecoded]
  extrude  "Extruded_192"  [1 undecoded]
  extrude  "Extruded_193"  [1 undecoded]
  extrude  "Extruded_194"  [1 undecoded]
  extrude  "Extruded_195"  [1 undecoded]
  extrude  "Extruded_196"  [1 undecoded]
  extrude  "Extruded_197"  [1 undecoded]
  extrude  "Extruded_198"  [1 undecoded]
  extrude  "Extruded_199"  [1 undecoded]
  extrude  "Extruded_200"  [1 undecoded]
  extrude  "Extruded_201"  [1 undecoded]
  extrude  "Extruded_202"  [1 undecoded]
  extrude  "Extruded_203"  [1 undecoded]
  extrude  "Extruded_204"  [1 undecoded]
  extrude  "Extruded_205"  [1 undecoded]
  extrude  "Extruded_206"  [1 undecoded]
  extrude  "Extruded_207"  [1 undecoded]
  extrude  "Extruded_208"  [1 undecoded]
  extrude  "Extruded_209"  [1 undecoded]
  extrude  "Extruded_210"  [1 undecoded]
  extrude  "Extruded_211"  [1 undecoded]
  extrude  "Extruded_212"  [1 undecoded]
  extrude  "Extruded_213"  [1 undecoded]
  extrude  "Extruded_214"  [1 undecoded]
  extrude  "Extruded_215"  [1 undecoded]
  extrude  "Extruded_216"  [1 undecoded]
  extrude  "Extruded_217"  [1 undecoded]
  extrude  "Extruded_218"  [1 undecoded]
  extrude  "Extruded_219"  [1 undecoded]
  extrude  "Extruded_220"  [1 undecoded]
  extrude  "Extruded_221"  [1 undecoded]
  extrude  "Extruded_222"  [1 undecoded]
  extrude  "Extruded_223"  [1 undecoded]
  extrude  "Extruded_224"  [1 undecoded]
  extrude  "Extruded_225"  [1 undecoded]
  extrude  "Extruded_226"  [1 undecoded]
  extrude  "Extruded_227"  [1 undecoded]
  extrude  "Extruded_228"  [1 undecoded]
  extrude  "Extruded_229"  [1 undecoded]
  extrude  "Extruded_230"  [1 undecoded]
  extrude  "Extruded_231"  [1 undecoded]
  extrude  "Extruded_232"  [1 undecoded]
  extrude  "Extruded_233"  [1 undecoded]
  extrude  "Extruded_234"  [1 undecoded]
  extrude  "Extruded_235"  [1 undecoded]
  extrude  "Extruded_236"  [1 undecoded]
  extrude  "Extruded_237"  [1 undecoded]
  extrude  "Extruded_238"  [1 undecoded]
  extrude  "Extruded_239"  [1 undecoded]
  extrude  "Extruded_240"  [1 undecoded]
  extrude  "Extruded_241"  [1 undecoded]
  extrude  "Extruded_242"  [1 undecoded]
  extrude  "Extruded_243"  [1 undecoded]
  extrude  "Extruded_244"  [1 undecoded]
  extrude  "Extruded_245"  [1 undecoded]
  extrude  "Extruded_246"  [1 undecoded]
  extrude  "Extruded_247"  [1 undecoded]
  extrude  "Extruded_248"  [1 undecoded]
  extrude  "Extruded_249"  [1 undecoded]
  extrude  "Extruded_250"  [1 undecoded]
  extrude  "Extruded_251"  [1 undecoded]
  extrude  "Extruded_252"  [1 undecoded]
  extrude  "Extruded_253"  [1 undecoded]
  extrude  "Extruded_254"  [1 undecoded]
  extrude  "Extruded_255"  [1 undecoded]
  extrude  "Extruded_256"  [1 undecoded]
  extrude  "Extruded_257"  [1 undecoded]
  extrude  "Extruded_258"  [1 undecoded]
  extrude  "Extruded_259"  [1 undecoded]
  extrude  "Extruded_260"  [1 undecoded]
  extrude  "Extruded_261"  [1 undecoded]
  extrude  "Extruded_262"  [1 undecoded]
  extrude  "Extruded_263"  [1 undecoded]
  extrude  "Extruded_264"  [1 undecoded]
  extrude  "Extruded_265"  [1 undecoded]
  extrude  "Extruded_266"  [1 undecoded]
  extrude  "Extruded_267"  [1 undecoded]
  extrude  "Extruded_268"  [1 undecoded]
  extrude  "Extruded_269"  [1 undecoded]
  extrude  "Extruded_270"  [1 undecoded]
  extrude  "Extruded_271"  [1 undecoded]
  extrude  "Extruded_272"  [1 undecoded]
  extrude  "Extruded_273"  [1 undecoded]
  extrude  "Extruded_274"  [1 undecoded]
  extrude  "Extruded_275"  [1 undecoded]
  extrude  "Extruded_276"  [1 undecoded]
  extrude  "Extruded_277"  [1 undecoded]
  extrude  "Extruded_278"  [1 undecoded]
  extrude  "Extruded_279"  [1 undecoded]
  extrude  "Extruded_280"  [1 undecoded]
  extrude  "Extruded_281"  [1 undecoded]
  extrude  "Extruded_282"  [1 undecoded]
  extrude  "Extruded_283"  [1 undecoded]
  extrude  "Extruded_284"  [1 undecoded]
  extrude  "Extruded_285"  [1 undecoded]
  extrude  "Extruded_286"  [1 undecoded]
  extrude  "Extruded_287"  [1 undecoded]
  extrude  "Extruded_288"  [1 undecoded]
  extrude  "Extruded_289"  [1 undecoded]
  extrude  "Extruded_290"  [1 undecoded]
  extrude  "Extruded_291"  [1 undecoded]
  extrude  "Extruded_292"  [1 undecoded]
  extrude  "Extruded_293"  [1 undecoded]
  extrude  "Extruded_294"  [1 undecoded]
  extrude  "Extruded_295"  [1 undecoded]
  extrude  "Extruded_296"  [1 undecoded]
  extrude  "Extruded_297"  [1 undecoded]
  extrude  "Extruded_298"  [1 undecoded]
  extrude  "Extruded_299"  [1 undecoded]
  extrude  "Extruded_300"  [1 undecoded]
  extrude  "Extruded_301"  [1 undecoded]
  extrude  "Extruded_302"  [1 undecoded]
  extrude  "Extruded_303"  [1 undecoded]
  extrude  "Extruded_304"  [1 undecoded]
  extrude  "Extruded_305"  [1 undecoded]
  extrude  "Extruded_306"  [1 undecoded]
  extrude  "Extruded_307"  [1 undecoded]
  extrude  "Extruded_308"  [1 undecoded]
  extrude  "Extruded_309"  [1 undecoded]
  extrude  "Extruded_310"  [1 undecoded]
  extrude  "Extruded_311"  [1 undecoded]
  extrude  "Extruded_312"  [1 undecoded]
  extrude  "Extruded_313"  [1 undecoded]
  extrude  "Extruded_314"  [1 undecoded]
  extrude  "Extruded_315"  [1 undecoded]
  extrude  "Extruded_316"  [1 undecoded]
  extrude  "Extruded_317"  [1 undecoded]
  extrude  "Extruded_318"  [1 undecoded]
  extrude  "Extruded_319"  [1 undecoded]
  extrude  "Extruded_320"  [1 undecoded]
  extrude  "Extruded_321"  [1 undecoded]
  extrude  "Extruded_322"  [1 undecoded]
  extrude  "Extruded_323"  [1 undecoded]
  extrude  "Extruded_324"  [1 undecoded]
  extrude  "Extruded_325"  [1 undecoded]
  extrude  "Extruded_326"  [1 undecoded]
  extrude  "Extruded_327"  [1 undecoded]
  extrude  "Extruded_328"  [1 undecoded]
  extrude  "Extruded_329"  [1 undecoded]
  extrude  "Extruded_330"  [1 undecoded]
  extrude  "Extruded_331"  [1 undecoded]
  extrude  "Extruded_332"  [1 undecoded]
  extrude  "Extruded_333"  [1 undecoded]
  extrude  "Extruded_334"  [1 undecoded]
  extrude  "Extruded_335"  [1 undecoded]
  extrude  "Extruded_336"  [1 undecoded]
  extrude  "Extruded_337"  [1 undecoded]
  extrude  "Extruded_338"  [1 undecoded]
  extrude  "Extruded_339"  [1 undecoded]
  extrude  "Extruded_340"  [1 undecoded]
  extrude  "Extruded_341"  [1 undecoded]
  extrude  "Extruded_342"  [1 undecoded]
  extrude  "Extruded_343"  [1 undecoded]
  extrude  "Extruded_344"  [1 undecoded]
  extrude  "Extruded_345"  [1 undecoded]
  extrude  "Extruded_346"  [1 undecoded]
  extrude  "Extruded_347"  [1 undecoded]
  extrude  "Extruded_348"  [1 undecoded]
  extrude  "Extruded_349"  [1 undecoded]
  extrude  "Extruded_350"  [1 undecoded]
  extrude  "Extruded_351"  [1 undecoded]
  extrude  "Extruded_352"  [1 undecoded]
  extrude  "Extruded_353"  [1 undecoded]
  extrude  "Extruded_354"  [1 undecoded]
  extrude  "Extruded_355"  [1 undecoded]
  extrude  "Extruded_356"  [1 undecoded]
  extrude  "Extruded_357"  [1 undecoded]
  extrude  "Extruded_358"  [1 undecoded]
  extrude  "Extruded_359"  [1 undecoded]
  extrude  "Extruded_360"  [1 undecoded]
  extrude  "Extruded_361"  [1 undecoded]
  extrude  "Extruded_362"  [1 undecoded]
  extrude  "Extruded_363"  [1 undecoded]
  extrude  "Extruded_364"  [1 undecoded]
  extrude  "Extruded_365"  [1 undecoded]
  extrude  "Extruded_366"  [1 undecoded]
  extrude  "Extruded_367"  [1 undecoded]
  extrude  "Extruded_368"  [1 undecoded]
  extrude  "Extruded_369"  [1 undecoded]
  extrude  "Extruded_370"  [1 undecoded]
  extrude  "Extruded_371"  [1 undecoded]
  extrude  "Extruded_372"  [1 undecoded]
  extrude  "Extruded_373"  [1 undecoded]
  extrude  "Extruded_374"  [1 undecoded]
  extrude  "Extruded_375"  [1 undecoded]
  extrude  "Extruded_376"  [1 undecoded]
  extrude  "Extruded_377"  [1 undecoded]
  extrude  "Extruded_378"  [1 undecoded]
  extrude  "Extruded_379"  [1 undecoded]
  extrude  "Extruded_380"  [1 undecoded]
  extrude  "Extruded_381"  [1 undecoded]
  extrude  "Extruded_382"  [1 undecoded]
  extrude  "Extruded_383"  [1 undecoded]
  extrude  "Extruded_384"  [1 undecoded]
  extrude  "Extruded_385"  [1 undecoded]
  extrude  "Extruded_386"  [1 undecoded]
  extrude  "Extruded_387"  [1 undecoded]
  extrude  "Extruded_388"  [1 undecoded]
  extrude  "Extruded_389"  [1 undecoded]
  extrude  "Extruded_390"  [1 undecoded]
  extrude  "Extruded_391"  [1 undecoded]
  extrude  "Extruded_392"  [1 undecoded]
  extrude  "Extruded_393"  [1 undecoded]
  extrude  "Extruded_394"  [1 undecoded]
  extrude  "Extruded_395"  [1 undecoded]
  extrude  "Extruded_396"  [1 undecoded]
  extrude  "Extruded_397"  [1 undecoded]
  extrude  "Extruded_398"  [1 undecoded]
  extrude  "Extruded_399"  [1 undecoded]
  extrude  "Extruded_400"  [1 undecoded]
  extrude  "Extruded_401"  [1 undecoded]
  extrude  "Extruded_402"  [1 undecoded]
  extrude  "Extruded_403"  [1 undecoded]
  extrude  "Extruded_404"  [1 undecoded]
  extrude  "Extruded_405"  [1 undecoded]
  extrude  "Extruded_406"  [1 undecoded]
  extrude  "Extruded_407"  [1 undecoded]
  extrude  "Extruded_408"  [1 undecoded]
  extrude  "Extruded_409"  [1 undecoded]
  extrude  "Extruded_410"  [1 undecoded]
  extrude  "Extruded_411"  [1 undecoded]
  extrude  "Extruded_412"  [1 undecoded]
  extrude  "Extruded_413"  [1 undecoded]
  extrude  "Extruded_414"  [1 undecoded]
  extrude  "Extruded_415"  [1 undecoded]
  extrude  "Extruded_416"  [1 undecoded]
  extrude  "Extruded_417"  [1 undecoded]
  extrude  "Extruded_418"  [1 undecoded]
  extrude  "Extruded_419"  [1 undecoded]
  extrude  "Extruded_420"  [1 undecoded]
  extrude  "Extruded_421"  [1 undecoded]
  extrude  "Extruded_422"  [1 undecoded]
  extrude  "Extruded_423"  [1 undecoded]
  extrude  "Extruded_424"  [1 undecoded]
  extrude  "Extruded_425"  [1 undecoded]
  extrude  "Extruded_426"  [1 undecoded]
  extrude  "Extruded_427"  [1 undecoded]
  extrude  "Extruded_428"  [1 undecoded]
  extrude  "Extruded_429"  [1 undecoded]
  extrude  "Extruded_430"  [1 undecoded]
  extrude  "Extruded_431"  [1 undecoded]
  extrude  "Extruded_432"  [1 undecoded]
  extrude  "Extruded_433"  [1 undecoded]
  extrude  "Extruded_434"  [1 undecoded]
  extrude  "Extruded_435"  [1 undecoded]
  extrude  "Extruded_436"  [1 undecoded]
  extrude  "Extruded_437"  [1 undecoded]
  extrude  "Extruded_438"  [1 undecoded]
  extrude  "Extruded_439"  [1 undecoded]
  extrude  "Extruded_440"  [1 undecoded]
  extrude  "Extruded_441"  [1 undecoded]
  extrude  "Extruded_442"  [1 undecoded]
  extrude  "Extruded_443"  [1 undecoded]
  extrude  "Extruded_444"  [1 undecoded]
  extrude  "Extruded_445"  [1 undecoded]
  extrude  "Extruded_446"  [1 undecoded]
  extrude  "Extruded_447"  [1 undecoded]
  extrude  "Extruded_448"  [1 undecoded]
  extrude  "Extruded_449"  [1 undecoded]
  extrude  "Extruded_450"  [1 undecoded]
  extrude  "Extruded_451"  [1 undecoded]
  extrude  "Extruded_452"  [1 undecoded]
  extrude  "Extruded_453"  [1 undecoded]
  extrude  "Extruded_454"  [1 undecoded]
  extrude  "Extruded_455"  [1 undecoded]
  extrude  "Extruded_456"  [1 undecoded]
  extrude  "Extruded_457"  [1 undecoded]
  extrude  "Extruded_458"  [1 undecoded]
  extrude  "Extruded_459"  [1 undecoded]
  extrude  "Extruded_460"  [1 undecoded]
  extrude  "Extruded_461"  [1 undecoded]
  extrude  "Extruded_462"  [1 undecoded]
  extrude  "Extruded_463"  [1 undecoded]
  extrude  "Extruded_464"  [1 undecoded]
  extrude  "Extruded_465"  [1 undecoded]
  extrude  "Extruded_466"  [1 undecoded]
  extrude  "Extruded_467"  [1 undecoded]
  extrude  "Extruded_468"  [1 undecoded]
  extrude  "Extruded_469"  [1 undecoded]
  extrude  "Extruded_470"  [1 undecoded]
  extrude  "Extruded_471"  [1 undecoded]
  extrude  "Extruded_472"  [1 undecoded]
  extrude  "Extruded_473"  [1 undecoded]
  extrude  "Extruded_474"  [1 undecoded]
  extrude  "Extruded_475"  [1 undecoded]
  extrude  "Extruded_476"  [1 undecoded]
  extrude  "Extruded_477"  [1 undecoded]
  extrude  "Extruded_478"  [1 undecoded]
  extrude  "Extruded_479"  [1 undecoded]
  extrude  "Extruded_480"  [1 undecoded]
  extrude  "Extruded_481"  [1 undecoded]
  extrude  "Extruded_482"  [1 undecoded]
  extrude  "Extruded_483"  [1 undecoded]
  extrude  "Extruded_484"  [1 undecoded]
  extrude  "Extruded_485"  [1 undecoded]
  extrude  "Extruded_486"  [1 undecoded]
  extrude  "Extruded_487"  [1 undecoded]
  extrude  "Extruded_488"  [1 undecoded]
  extrude  "Extruded_489"  [1 undecoded]
  extrude  "Extruded_490"  [1 undecoded]
  extrude  "Extruded_491"  [1 undecoded]
  extrude  "Extruded_492"  [1 undecoded]
  extrude  "Extruded_493"  [1 undecoded]
  extrude  "Extruded_494"  [1 undecoded]
  extrude  "Extruded_495"  [1 undecoded]
  extrude  "Extruded_496"  [1 undecoded]
  extrude  "Extruded_497"  [1 undecoded]
  extrude  "Extruded_498"  [1 undecoded]
  extrude  "Extruded_499"  [1 undecoded]
  extrude  "Extruded_500"  [1 undecoded]
  extrude  "Extruded_501"  [1 undecoded]
  extrude  "Extruded_502"  [1 undecoded]
  extrude  "Extruded_503"  [1 undecoded]
  extrude  "Extruded_504"  [1 undecoded]
  extrude  "Extruded_505"  [1 undecoded]
  extrude  "Extruded_506"  [1 undecoded]
  extrude  "Extruded_507"  [1 undecoded]
  extrude  "Extruded_508"  [1 undecoded]
  extrude  "Extruded_509"  [1 undecoded]
  extrude  "Extruded_510"  [1 undecoded]
  extrude  "Extruded_511"  [1 undecoded]
  extrude  "Extruded_512"  [1 undecoded]
  extrude  "Extruded_513"  [1 undecoded]
  extrude  "Extruded_514"  [1 undecoded]
  extrude  "Extruded_515"  [1 undecoded]
  extrude  "Extruded_516"  [1 undecoded]
  extrude  "Extruded_517"  [1 undecoded]
  extrude  "Extruded_518"  [1 undecoded]
  extrude  "Extruded_519"  [1 undecoded]
  extrude  "Extruded_520"  [1 undecoded]
  extrude  "Extruded_521"  [1 undecoded]
  extrude  "Extruded_522"  [1 undecoded]
  extrude  "Extruded_523"  [1 undecoded]
  extrude  "Extruded_524"  [1 undecoded]
  extrude  "Extruded_525"  [1 undecoded]
  extrude  "Extruded_526"  [1 undecoded]
  extrude  "Extruded_527"  [1 undecoded]
  extrude  "Extruded_528"  [1 undecoded]
  extrude  "Extruded_529"  [1 undecoded]
  extrude  "Extruded_530"  [1 undecoded]
  extrude  "Extruded_531"  [1 undecoded]
  extrude  "Extruded_532"  [1 undecoded]
  extrude  "Extruded_533"  [1 undecoded]
  extrude  "Extruded_534"  [1 undecoded]
  extrude  "Extruded_535"  [1 undecoded]
  extrude  "Extruded_536"  [1 undecoded]
  extrude  "Extruded_537"  [1 undecoded]
  extrude  "Extruded_538"  [1 undecoded]
  extrude  "Extruded_539"  [1 undecoded]
  extrude  "Extruded_540"  [1 undecoded]
  extrude  "Extruded_541"  [1 undecoded]
  extrude  "Extruded_542"  [1 undecoded]
  extrude  "Extruded_543"  [1 undecoded]
  extrude  "Extruded_544"  [1 undecoded]
  extrude  "Extruded_545"  [1 undecoded]
  extrude  "Extruded_546"  [1 undecoded]
  extrude  "Extruded_547"  [1 undecoded]
  extrude  "Extruded_548"  [1 undecoded]
  extrude  "Extruded_549"  [1 undecoded]
  extrude  "Extruded_550"  [1 undecoded]
  extrude  "Extruded_551"  [1 undecoded]
  extrude  "Extruded_552"  [1 undecoded]
  extrude  "Extruded_553"  [1 undecoded]
  extrude  "Extruded_554"  [1 undecoded]
  extrude  "Extruded_555"  [1 undecoded]
  extrude  "Extruded_556"  [1 undecoded]
  extrude  "Extruded_557"  [1 undecoded]
  extrude  "Extruded_558"  [1 undecoded]
  extrude  "Extruded_559"  [1 undecoded]
  extrude  "Extruded_560"  [1 undecoded]
  extrude  "Extruded_561"  [1 undecoded]
  extrude  "Extruded_562"  [1 undecoded]
  extrude  "Extruded_563"  [1 undecoded]
  extrude  "Extruded_564"  [1 undecoded]
  extrude  "Extruded_565"  [1 undecoded]
  extrude  "Extruded_566"  [1 undecoded]
  extrude  "Extruded_567"  [1 undecoded]
  extrude  "Extruded_568"  [1 undecoded]
  extrude  "Extruded_569"  [1 undecoded]
  extrude  "Extruded_570"  [1 undecoded]
  extrude  "Extruded_571"  [1 undecoded]
  extrude  "Extruded_572"  [1 undecoded]
  extrude  "Extruded_573"  [1 undecoded]
  extrude  "Extruded_574"  [1 undecoded]
  extrude  "Extruded_575"  [1 undecoded]
  extrude  "Extruded_576"  [1 undecoded]
  extrude  "Extruded_577"  [1 undecoded]
  extrude  "Extruded_578"  [1 undecoded]
  extrude  "Extruded_579"  [1 undecoded]
  extrude  "Extruded_580"  [1 undecoded]
  extrude  "Extruded_581"  [1 undecoded]
  extrude  "Extruded_582"  [1 undecoded]
  extrude  "Extruded_583"  [1 undecoded]
  extrude  "Extruded_584"  [1 undecoded]
  extrude  "Extruded_585"  [1 undecoded]
  extrude  "Extruded_586"  [1 undecoded]
  extrude  "Extruded_587"  [1 undecoded]
  extrude  "Extruded_588"  [1 undecoded]
  extrude  "Extruded_589"  [1 undecoded]
  extrude  "Extruded_590"  [1 undecoded]
  extrude  "Extruded_591"  [1 undecoded]
  extrude  "Extruded_592"  [1 undecoded]
  extrude  "Extruded_593"  [1 undecoded]
  extrude  "Extruded_594"  [1 undecoded]
  extrude  "Extruded_595"  [1 undecoded]
  extrude  "Extruded_596"  [1 undecoded]
  extrude  "Extruded_597"  [1 undecoded]
  extrude  "Extruded_598"  [1 undecoded]
  extrude  "Extruded_599"  [1 undecoded]
  extrude  "Extruded_600"  [1 undecoded]
  extrude  "Extruded_601"  [1 undecoded]
  extrude  "Extruded_602"  [1 undecoded]
  extrude  "Extruded_603"  [1 undecoded]
  extrude  "Extruded_604"  [1 undecoded]
  extrude  "Extruded_605"  [1 undecoded]
  extrude  "Extruded_606"  [1 undecoded]
  extrude  "Extruded_607"  [1 undecoded]
  extrude  "Extruded_608"  [1 undecoded]
  extrude  "Extruded_609"  [1 undecoded]
  extrude  "Extruded_610"  [1 undecoded]
  extrude  "Extruded_611"  [1 undecoded]
  extrude  "Extruded_612"  [1 undecoded]
  extrude  "Extruded_613"  [1 undecoded]
  extrude  "Extruded_614"  [1 undecoded]
  extrude  "Extruded_615"  [1 undecoded]
  extrude  "Extruded_616"  [1 undecoded]
  extrude  "Extruded_617"  [1 undecoded]
  extrude  "Extruded_618"  [1 undecoded]
  extrude  "Extruded_619"  [1 undecoded]
  extrude  "Extruded_620"  [1 undecoded]
  extrude  "Extruded_621"  [1 undecoded]
  extrude  "Extruded_622"  [1 undecoded]
  extrude  "Extruded_623"  [1 undecoded]
  extrude  "Extruded_624"  [1 undecoded]
  extrude  "Extruded_625"  [1 undecoded]
  extrude  "Extruded_626"  [1 undecoded]
  extrude  "Extruded_627"  [1 undecoded]
  extrude  "Extruded_628"  [1 undecoded]
  extrude  "Extruded_629"  [1 undecoded]
  extrude  "Extruded_630"  [1 undecoded]
  extrude  "Extruded_631"  [1 undecoded]
  extrude  "Extruded_632"  [1 undecoded]
  extrude  "Extruded_633"  [1 undecoded]
  extrude  "Extruded_634"  [1 undecoded]
  extrude  "Extruded_635"  [1 undecoded]
  extrude  "Extruded_636"  [1 undecoded]
  extrude  "Extruded_637"  [1 undecoded]
  extrude  "Extruded_638"  [1 undecoded]
  extrude  "Extruded_639"  [1 undecoded]
  extrude  "Extruded_640"  [1 undecoded]
  extrude  "Extruded_641"  [1 undecoded]
  other  "Cylinder_8"
  extrude  "Extruded_642"  [1 undecoded]
  extrude  "Extruded_643"  [1 undecoded]
  extrude  "Extruded_644"  [1 undecoded]
  extrude  "Extruded_645"  [1 undecoded]
  extrude  "Extruded_646"  [1 undecoded]
  extrude  "Extruded_647"  [1 undecoded]
  extrude  "Extruded_648"  [1 undecoded]
  extrude  "Extruded_649"  [1 undecoded]
  extrude  "Extruded_650"  [1 undecoded]
  extrude  "Extruded_651"  [1 undecoded]
  extrude  "Extruded_652"  [1 undecoded]
  extrude  "Extruded_653"  [1 undecoded]
  extrude  "Extruded_654"  [1 undecoded]
  extrude  "Extruded_655"  [1 undecoded]
  extrude  "Extruded_656"  [1 undecoded]
  extrude  "Extruded_657"  [1 undecoded]
  extrude  "Extruded_658"  [1 undecoded]
  extrude  "Extruded_659"  [1 undecoded]
  extrude  "Extruded_660"  [1 undecoded]
  extrude  "Extruded_661"  [1 undecoded]
  extrude  "Extruded_662"  [1 undecoded]
  extrude  "Extruded_663"  [1 undecoded]
  extrude  "Extruded_664"  [1 undecoded]
  other  "Open CASCADE STEP translator 6.2 1.226.1.1"
  extrude  "Extruded_665"  [1 undecoded]
  extrude  "Extruded_666"  [1 undecoded]
  extrude  "Extruded_667"  [1 undecoded]
  extrude  "Extruded_668"  [1 undecoded]
  extrude  "Extruded_669"  [1 undecoded]
  extrude  "Extruded_670"  [1 undecoded]
  extrude  "Extruded_671"  [1 undecoded]
  extrude  "Extruded_672"  [1 undecoded]
  extrude  "Extruded_673"  [1 undecoded]
  extrude  "Extruded_674"  [1 undecoded]
  extrude  "Extruded_675"  [1 undecoded]
  extrude  "Extruded_676"  [1 undecoded]
  extrude  "Extruded_677"  [1 undecoded]
  extrude  "Extruded_678"  [1 undecoded]
  extrude  "Extruded_679"  [1 undecoded]
  extrude  "Extruded_680"  [1 undecoded]
  extrude  "Extruded_681"  [1 undecoded]
  extrude  "Extruded_682"  [1 undecoded]
  extrude  "Extruded_683"  [1 undecoded]
  extrude  "Extruded_684"  [1 undecoded]
  extrude  "Extruded_685"  [1 undecoded]
  extrude  "Extruded_686"  [1 undecoded]
  extrude  "Extruded_687"  [1 undecoded]
  extrude  "Extruded_688"  [1 undecoded]
  extrude  "Extruded_689"  [1 undecoded]
  extrude  "Extruded_690"  [1 undecoded]
  extrude  "Extruded_691"  [1 undecoded]
  extrude  "Extruded_692"  [1 undecoded]
  extrude  "Extruded_693"  [1 undecoded]
  extrude  "Extruded_694"  [1 undecoded]
  extrude  "Extruded_695"  [1 undecoded]
  extrude  "Extruded_696"  [1 undecoded]
  extrude  "Extruded_697"  [1 undecoded]
  extrude  "Extruded_698"  [1 undecoded]
  extrude  "Extruded_699"  [1 undecoded]
  extrude  "Extruded_700"  [1 undecoded]
  extrude  "Extruded_701"  [1 undecoded]
  extrude  "Extruded_702"  [1 undecoded]
  extrude  "Extruded_703"  [1 undecoded]
  extrude  "Extruded_704"  [1 undecoded]
  other  "Cylinder_9"
  other  "Cylinder_10"
  other  "Cylinder_11"
  other  "Cylinder_12"
  other  "Cylinder_13"
  other  "Cylinder_14"
  other  "Cylinder_15"
  other  "Cylinder_16"
  other  "Cylinder_17"
  other  "Cylinder_18"
  other  "Cylinder_19"
  other  "Cylinder_20"
  other  "Cylinder_21"
  other  "Cylinder_22"
  other  "Cylinder_23"
  other  "Cylinder_24"
  other  "Cylinder_25"
  other  "Cylinder_26"
  other  "Cylinder_27"
  other  "Cylinder_28"
  extrude  "Extruded_705"  [1 undecoded]
  other  "Cylinder_29"
  other  "Cylinder_30"
  extrude  "Extruded_706"  [1 undecoded]
  extrude  "Extruded_707"  [1 undecoded]
  extrude  "Extruded_708"  [1 undecoded]
  extrude  "Extruded_709"  [1 undecoded]
  extrude  "Extruded_710"  [1 undecoded]
  extrude  "Extruded_711"  [1 undecoded]
  extrude  "Extruded_712"  [1 undecoded]
  extrude  "Extruded_713"  [1 undecoded]
  extrude  "Extruded_714"  [1 undecoded]
  extrude  "Extruded_715"  [1 undecoded]
  extrude  "Extruded_716"  [1 undecoded]
  extrude  "Extruded_717"  [1 undecoded]
  extrude  "Extruded_718"  [1 undecoded]
  extrude  "Extruded_719"  [1 undecoded]
  extrude  "Extruded_720"  [1 undecoded]
  extrude  "Extruded_721"  [1 undecoded]
  extrude  "Extruded_722"  [1 undecoded]
  other  "Open CASCADE STEP translator 6.2 1.229.1.1"
  extrude  "Extruded_723"  [1 undecoded]
  extrude  "Extruded_724"  [1 undecoded]
  extrude  "Extruded_725"  [1 undecoded]
  extrude  "Extruded_726"  [1 undecoded]
  extrude  "Extruded_727"  [1 undecoded]
  extrude  "Extruded_728"  [1 undecoded]
  extrude  "Extruded_729"  [1 undecoded]
  extrude  "Extruded_730"  [1 undecoded]
  extrude  "Extruded_731"  [1 undecoded]
  extrude  "Extruded_732"  [1 undecoded]
  extrude  "Extruded_733"  [1 undecoded]
  extrude  "Extruded_734"  [1 undecoded]
  other  "61082101400lf"
  other  "61082101400lf_1"
  extrude  "Extruded_735"  [1 undecoded]
  extrude  "Extruded_736"  [1 undecoded]
  extrude  "Extruded_737"  [1 undecoded]
  extrude  "Extruded_738"  [1 undecoded]
  extrude  "Extruded_739"  [1 undecoded]
  extrude  "Extruded_740"  [1 undecoded]
  extrude  "Extruded_741"  [1 undecoded]
  extrude  "Extruded_742"  [1 undecoded]
  extrude  "Extruded_743"  [1 undecoded]
  extrude  "Extruded_744"  [1 undecoded]
  extrude  "Extruded_745"  [1 undecoded]
  extrude  "Extruded_746"  [1 undecoded]
  extrude  "Extruded_747"  [1 undecoded]
  extrude  "Extruded_748"  [1 undecoded]
  extrude  "Extruded_749"  [1 undecoded]
  extrude  "Extruded_750"  [1 undecoded]
  extrude  "Extruded_751"  [1 undecoded]
  extrude  "Extruded_752"  [1 undecoded]
  extrude  "Extruded_753"  [1 undecoded]
  extrude  "Extruded_754"  [1 undecoded]
  extrude  "Extruded_755"  [1 undecoded]
  extrude  "Extruded_756"  [1 undecoded]
  extrude  "Extruded_757"  [1 undecoded]
  extrude  "Extruded_758"  [1 undecoded]
  extrude  "Extruded_759"  [1 undecoded]
  extrude  "Extruded_760"  [1 undecoded]
  extrude  "Extruded_761"  [1 undecoded]
  extrude  "Extruded_762"  [1 undecoded]
  extrude  "Extruded_763"  [1 undecoded]
  extrude  "Extruded_764"  [1 undecoded]
  extrude  "Extruded_765"  [1 undecoded]
  extrude  "Extruded_766"  [1 undecoded]
  extrude  "Extruded_767"  [1 undecoded]
  extrude  "Extruded_768"  [1 undecoded]
  extrude  "Extruded_769"  [1 undecoded]
  extrude  "Extruded_770"  [1 undecoded]
  extrude  "Extruded_771"  [1 undecoded]
  extrude  "Extruded_772"  [1 undecoded]
  extrude  "Extruded_773"  [1 undecoded]
  extrude  "Extruded_774"  [1 undecoded]
  extrude  "Extruded_775"  [1 undecoded]
  extrude  "Extruded_776"  [1 undecoded]
  extrude  "Extruded_777"  [1 undecoded]
  extrude  "Extruded_778"  [1 undecoded]
  extrude  "Extruded_779"  [1 undecoded]
  extrude  "Extruded_780"  [1 undecoded]
  extrude  "Extruded_781"  [1 undecoded]
  extrude  "Extruded_782"  [1 undecoded]
  extrude  "Extruded_783"  [1 undecoded]
  extrude  "Extruded_784"  [1 undecoded]
  extrude  "Extruded_785"  [1 undecoded]
  extrude  "Extruded_786"  [1 undecoded]
  extrude  "Extruded_787"  [1 undecoded]
  extrude  "Extruded_788"  [1 undecoded]
  extrude  "Extruded_789"  [1 undecoded]
  extrude  "Extruded_790"  [1 undecoded]
  extrude  "Extruded_791"  [1 undecoded]
  extrude  "Extruded_792"  [1 undecoded]
  extrude  "Extruded_793"  [1 undecoded]
  extrude  "Extruded_794"  [1 undecoded]
  extrude  "Extruded_795"  [1 undecoded]
  extrude  "Extruded_796"  [1 undecoded]
  extrude  "Extruded_797"  [1 undecoded]
  extrude  "Extruded_798"  [1 undecoded]
  extrude  "Extruded_799"  [1 undecoded]
  extrude  "Extruded_800"  [1 undecoded]
  extrude  "Extruded_801"  [1 undecoded]
  extrude  "Extruded_802"  [1 undecoded]
  extrude  "Extruded_803"  [1 undecoded]
  extrude  "Extruded_804"  [1 undecoded]
  extrude  "Extruded_805"  [1 undecoded]
  extrude  "Extruded_806"  [1 undecoded]
  extrude  "Extruded_807"  [1 undecoded]
  extrude  "Extruded_808"  [1 undecoded]
  extrude  "Extruded_809"  [1 undecoded]
  extrude  "Extruded_810"  [1 undecoded]
  extrude  "Extruded_811"  [1 undecoded]
  extrude  "Extruded_812"  [1 undecoded]
  extrude  "Extruded_813"  [1 undecoded]
  extrude  "Extruded_814"  [1 undecoded]
  extrude  "Extruded_815"  [1 undecoded]
  extrude  "Extruded_816"  [1 undecoded]
  extrude  "Extruded_817"  [1 undecoded]
  extrude  "Extruded_818"  [1 undecoded]
  extrude  "Extruded_819"  [1 undecoded]
  extrude  "Extruded_820"  [1 undecoded]
  extrude  "Extruded_821"  [1 undecoded]
  extrude  "Extruded_822"  [1 undecoded]
  extrude  "Extruded_823"  [1 undecoded]
  extrude  "Extruded_824"  [1 undecoded]
  extrude  "Extruded_825"  [1 undecoded]
  extrude  "Extruded_826"  [1 undecoded]
  extrude  "Extruded_827"  [1 undecoded]
  extrude  "Extruded_828"  [1 undecoded]
  extrude  "Extruded_829"  [1 undecoded]
  extrude  "Extruded_830"  [1 undecoded]
  extrude  "Extruded_831"  [1 undecoded]
  extrude  "Extruded_832"  [1 undecoded]
  extrude  "Extruded_833"  [1 undecoded]
  extrude  "Extruded_834"  [1 undecoded]
  extrude  "Extruded_835"  [1 undecoded]
  extrude  "Extruded_836"  [1 undecoded]
  extrude  "Extruded_837"  [1 undecoded]
  extrude  "Extruded_838"  [1 undecoded]
  extrude  "Extruded_839"  [1 undecoded]
  extrude  "Extruded_840"  [1 undecoded]
  extrude  "Extruded_841"  [1 undecoded]
  extrude  "Extruded_842"  [1 undecoded]
  extrude  "Extruded_843"  [1 undecoded]
  extrude  "Extruded_844"  [1 undecoded]
  extrude  "Extruded_845"  [1 undecoded]
  extrude  "Extruded_846"  [1 undecoded]
  extrude  "Extruded_847"  [1 undecoded]
  extrude  "Extruded_848"  [1 undecoded]
  extrude  "Extruded_849"  [1 undecoded]
  extrude  "Extruded_850"  [1 undecoded]
  extrude  "Extruded_851"  [1 undecoded]
  extrude  "Extruded_852"  [1 undecoded]
  extrude  "Extruded_853"  [1 undecoded]
  extrude  "Extruded_854"  [1 undecoded]
  extrude  "Extruded_855"  [1 undecoded]
  extrude  "Extruded_856"  [1 undecoded]
  extrude  "Extruded_857"  [1 undecoded]
  extrude  "Extruded_858"  [1 undecoded]
  extrude  "Extruded_859"  [1 undecoded]
  extrude  "Extruded_860"  [1 undecoded]
  extrude  "Extruded_861"  [1 undecoded]
  extrude  "Extruded_862"  [1 undecoded]
  extrude  "Extruded_863"  [1 undecoded]
  extrude  "Extruded_864"  [1 undecoded]
  extrude  "Extruded_865"  [1 undecoded]
  extrude  "Extruded_866"  [1 undecoded]
  extrude  "Extruded_867"  [1 undecoded]
  extrude  "Extruded_868"  [1 undecoded]
  extrude  "Extruded_869"  [1 undecoded]
  extrude  "Extruded_870"  [1 undecoded]
  extrude  "Extruded_871"  [1 undecoded]
  extrude  "Extruded_872"  [1 undecoded]
  extrude  "Extruded_873"  [1 undecoded]
  extrude  "Extruded_874"  [1 undecoded]
  extrude  "Extruded_875"  [1 undecoded]
  extrude  "Extruded_876"  [1 undecoded]
  extrude  "Extruded_877"  [1 undecoded]
  extrude  "Extruded_878"  [1 undecoded]
  extrude  "Extruded_879"  [1 undecoded]
  extrude  "Extruded_880"  [1 undecoded]
  extrude  "Extruded_881"  [1 undecoded]
  extrude  "Extruded_882"  [1 undecoded]
  extrude  "Extruded_883"  [1 undecoded]
  extrude  "Extruded_884"  [1 undecoded]
  extrude  "Extruded_885"  [1 undecoded]
  extrude  "Extruded_886"  [1 undecoded]
  extrude  "Extruded_887"  [1 undecoded]
  extrude  "Extruded_888"  [1 undecoded]
  extrude  "Extruded_889"  [1 undecoded]
  extrude  "Extruded_890"  [1 undecoded]
  extrude  "Extruded_891"  [1 undecoded]
  extrude  "Extruded_892"  [1 undecoded]
  extrude  "Extruded_893"  [1 undecoded]
  extrude  "Extruded_894"  [1 undecoded]
  extrude  "Extruded_895"  [1 undecoded]
  extrude  "Extruded_896"  [1 undecoded]
  extrude  "Extruded_897"  [1 undecoded]
  extrude  "Extruded_898"  [1 undecoded]
  extrude  "Extruded_899"  [1 undecoded]
  extrude  "Extruded_900"  [1 undecoded]
  extrude  "Extruded_901"  [1 undecoded]
  extrude  "Extruded_902"  [1 undecoded]
  extrude  "Extruded_903"  [1 undecoded]
  extrude  "Extruded_904"  [1 undecoded]
  extrude  "Extruded_905"  [1 undecoded]
  extrude  "Extruded_906"  [1 undecoded]
  extrude  "Extruded_907"  [1 undecoded]
  extrude  "Extruded_908"  [1 undecoded]
  extrude  "Extruded_909"  [1 undecoded]
  extrude  "Extruded_910"  [1 undecoded]
  extrude  "Extruded_911"  [1 undecoded]
  extrude  "Extruded_912"  [1 undecoded]
  extrude  "Extruded_913"  [1 undecoded]
  extrude  "Extruded_914"  [1 undecoded]
  extrude  "Extruded_915"  [1 undecoded]
  extrude  "Extruded_916"  [1 undecoded]
  extrude  "Extruded_917"  [1 undecoded]
  extrude  "Extruded_918"  [1 undecoded]
  extrude  "Extruded_919"  [1 undecoded]
  extrude  "Extruded_920"  [1 undecoded]
  extrude  "Extruded_921"  [1 undecoded]
  extrude  "Extruded_922"  [1 undecoded]
  extrude  "Extruded_923"  [1 undecoded]
  extrude  "Extruded_924"  [1 undecoded]
  extrude  "Extruded_925"  [1 undecoded]
  extrude  "Extruded_926"  [1 undecoded]
  extrude  "Extruded_927"  [1 undecoded]
  extrude  "Extruded_928"  [1 undecoded]
  extrude  "Extruded_929"  [1 undecoded]
  extrude  "Extruded_930"  [1 undecoded]
  extrude  "Extruded_931"  [1 undecoded]
  extrude  "Extruded_932"  [1 undecoded]
  extrude  "Extruded_933"  [1 undecoded]
  extrude  "Extruded_934"  [1 undecoded]
  extrude  "Extruded_935"  [1 undecoded]
  extrude  "Extruded_936"  [1 undecoded]
  extrude  "Extruded_937"  [1 undecoded]
  extrude  "Extruded_938"  [1 undecoded]
  extrude  "Extruded_939"  [1 undecoded]
  extrude  "Extruded_940"  [1 undecoded]
  extrude  "Extruded_941"  [1 undecoded]
  extrude  "Extruded_942"  [1 undecoded]
  extrude  "Extruded_943"  [1 undecoded]
  extrude  "Extruded_944"  [1 undecoded]
  extrude  "Extruded_945"  [1 undecoded]
  extrude  "Extruded_946"  [1 undecoded]
  extrude  "Extruded_947"  [1 undecoded]
  extrude  "Extruded_948"  [1 undecoded]
  extrude  "Extruded_949"  [1 undecoded]
  extrude  "Extruded_950"  [1 undecoded]
  extrude  "Extruded_951"  [1 undecoded]
  extrude  "Extruded_952"  [1 undecoded]
  extrude  "Extruded_953"  [1 undecoded]
  extrude  "Extruded_954"  [1 undecoded]
  extrude  "Extruded_955"  [1 undecoded]
  extrude  "Extruded_956"  [1 undecoded]
  extrude  "Extruded_957"  [1 undecoded]
  extrude  "Extruded_958"  [1 undecoded]
  extrude  "Extruded_959"  [1 undecoded]
  extrude  "Extruded_960"  [1 undecoded]
  extrude  "Extruded_961"  [1 undecoded]
  extrude  "Extruded_962"  [1 undecoded]
  extrude  "Extruded_963"  [1 undecoded]
  extrude  "Extruded_964"  [1 undecoded]
  extrude  "Extruded_965"  [1 undecoded]
  extrude  "Extruded_966"  [1 undecoded]
  extrude  "Extruded_967"  [1 undecoded]
  extrude  "Extruded_968"  [1 undecoded]
  extrude  "Extruded_969"  [1 undecoded]
  extrude  "Extruded_970"  [1 undecoded]
  extrude  "Extruded_971"  [1 undecoded]
  extrude  "Extruded_972"  [1 undecoded]
  extrude  "Extruded_973"  [1 undecoded]
  extrude  "Extruded_974"  [1 undecoded]
  extrude  "Extruded_975"  [1 undecoded]
  extrude  "Extruded_976"  [1 undecoded]
  extrude  "Extruded_977"  [1 undecoded]
  extrude  "Extruded_978"  [1 undecoded]
  extrude  "Extruded_979"  [1 undecoded]
  extrude  "Extruded_980"  [1 undecoded]
  extrude  "Extruded_981"  [1 undecoded]
  extrude  "Extruded_982"  [1 undecoded]
  extrude  "Extruded_983"  [1 undecoded]
  extrude  "Extruded_984"  [1 undecoded]
  extrude  "Extruded_985"  [1 undecoded]
  extrude  "Extruded_986"  [1 undecoded]
  extrude  "Extruded_987"  [1 undecoded]
  extrude  "Extruded_988"  [1 undecoded]
  extrude  "Extruded_989"  [1 undecoded]
  extrude  "Extruded_990"  [1 undecoded]
  extrude  "Extruded_991"  [1 undecoded]
  extrude  "Extruded_992"  [1 undecoded]
  extrude  "Extruded_993"  [1 undecoded]
  extrude  "Extruded_994"  [1 undecoded]
  extrude  "Extruded_995"  [1 undecoded]
  extrude  "Extruded_996"  [1 undecoded]
  extrude  "Extruded_997"  [1 undecoded]
  extrude  "Extruded_998"  [1 undecoded]
  extrude  "Extruded_999"  [1 undecoded]
  extrude  "Extruded_1000"  [1 undecoded]
  extrude  "Extruded_1001"  [1 undecoded]
  extrude  "Extruded_1002"  [1 undecoded]
  extrude  "Extruded_1003"  [1 undecoded]
  extrude  "Extruded_1004"  [1 undecoded]
  extrude  "Extruded_1005"  [1 undecoded]
  extrude  "Extruded_1006"  [1 undecoded]
  extrude  "Extruded_1007"  [1 undecoded]
  extrude  "Extruded_1008"  [1 undecoded]
  extrude  "Extruded_1009"  [1 undecoded]
  extrude  "Extruded_1010"  [1 undecoded]
  extrude  "Extruded_1011"  [1 undecoded]
  extrude  "Extruded_1012"  [1 undecoded]
  extrude  "Extruded_1013"  [1 undecoded]
  extrude  "Extruded_1014"  [1 undecoded]
  extrude  "Extruded_1015"  [1 undecoded]
  extrude  "Extruded_1016"  [1 undecoded]
  extrude  "Extruded_1017"  [1 undecoded]
  extrude  "Extruded_1018"  [1 undecoded]
  other  "Cylinder_31"
  extrude  "Extruded_1019"  [1 undecoded]
  other  "Cylinder_32"
  other  "Cylinder_33"
  extrude  "Extruded_1020"  [1 undecoded]
  other  "Cylinder_34"
  extrude  "Extruded_1021"  [1 undecoded]
  extrude  "Extruded_1022"  [1 undecoded]
  other  "Cylinder_35"
  extrude  "Extruded_1023"  [1 undecoded]
  other  "Cylinder_36"
  other  "Cylinder_37"
  extrude  "Extruded_1024"  [1 undecoded]
  extrude  "Extruded_1025"  [1 undecoded]
  other  "Cylinder_38"
  extrude  "Extruded_1026"  [1 undecoded]
  extrude  "Extruded_1027"  [1 undecoded]
  extrude  "Extruded_1028"  [1 undecoded]
  extrude  "Extruded_1029"  [1 undecoded]
  extrude  "Extruded_1030"  [1 undecoded]
  extrude  "Extruded_1031"  [1 undecoded]
  other  "Cylinder_39"
  extrude  "Extruded_1032"  [1 undecoded]
  extrude  "Extruded_1033"  [1 undecoded]
  other  "Cylinder_40"
  extrude  "Extruded_1034"  [1 undecoded]
  other  "Cylinder_41"
  extrude  "Extruded_1035"  [1 undecoded]
  other  "Cylinder_42"
  extrude  "Extruded_1036"  [1 undecoded]
  other  "Cylinder_43"
  extrude  "Extruded_1037"  [1 undecoded]
  other  "Cylinder_44"
  extrude  "Extruded_1038"  [1 undecoded]
  extrude  "Extruded_1039"  [1 undecoded]
  extrude  "Extruded_1040"  [1 undecoded]
  extrude  "Extruded_1041"  [1 undecoded]
  extrude  "Extruded_1042"  [1 undecoded]
  extrude  "Extruded_1043"  [1 undecoded]
  extrude  "Extruded_1044"  [1 undecoded]
  extrude  "Extruded_1045"  [1 undecoded]
  extrude  "Extruded_1046"  [1 undecoded]
  extrude  "Extruded_1047"  [1 undecoded]
  extrude  "Extruded_1048"  [1 undecoded]
  extrude  "Extruded_1049"  [1 undecoded]
  extrude  "Extruded_1050"  [1 undecoded]
  extrude  "Extruded_1051"  [1 undecoded]
  extrude  "Extruded_1052"  [1 undecoded]
  extrude  "Extruded_1053"  [1 undecoded]
  extrude  "Extruded_1054"  [1 undecoded]
  extrude  "Extruded_1055"  [1 undecoded]
  extrude  "Extruded_1056"  [1 undecoded]
  extrude  "Extruded_1057"  [1 undecoded]
  extrude  "Extruded_1058"  [1 undecoded]
  extrude  "Extruded_1059"  [1 undecoded]
  extrude  "Extruded_1060"  [1 undecoded]
  extrude  "Extruded_1061"  [1 undecoded]
  extrude  "Extruded_1062"  [1 undecoded]
  extrude  "Extruded_1063"  [1 undecoded]
  extrude  "Extruded_1064"  [1 undecoded]
  extrude  "Extruded_1065"  [1 undecoded]
  extrude  "Extruded_1066"  [1 undecoded]
  other  "Cylinder_45"
  extrude  "Extruded_1067"  [1 undecoded]
  extrude  "Extruded_1068"  [1 undecoded]
  extrude  "Extruded_1069"  [1 undecoded]
  extrude  "Extruded_1070"  [1 undecoded]
  extrude  "Extruded_1071"  [1 undecoded]
  extrude  "Extruded_1072"  [1 undecoded]
  extrude  "Extruded_1073"  [1 undecoded]
  extrude  "Extruded_1074"  [1 undecoded]
  extrude  "Extruded_1075"  [1 undecoded]
  extrude  "Extruded_1076"  [1 undecoded]
  extrude  "Extruded_1077"  [1 undecoded]
  extrude  "Extruded_1078"  [1 undecoded]
  extrude  "Extruded_1079"  [1 undecoded]
  extrude  "Extruded_1080"  [1 undecoded]
  extrude  "Extruded_1081"  [1 undecoded]
  extrude  "Extruded_1082"  [1 undecoded]
  extrude  "Extruded_1083"  [1 undecoded]
  extrude  "Extruded_1084"  [1 undecoded]
  extrude  "Extruded_1085"  [1 undecoded]
  extrude  "Extruded_1086"  [1 undecoded]
  extrude  "Extruded_1087"  [1 undecoded]
  extrude  "Extruded_1088"  [1 undecoded]
  extrude  "Extruded_1089"  [1 undecoded]
  extrude  "Extruded_1090"  [1 undecoded]
  extrude  "Extruded_1091"  [1 undecoded]
  extrude  "Extruded_1092"  [1 undecoded]
  extrude  "Extruded_1093"  [1 undecoded]
  extrude  "Extruded_1094"  [1 undecoded]
  extrude  "Extruded_1095"  [1 undecoded]
  extrude  "Extruded_1096"  [1 undecoded]
  extrude  "Extruded_1097"  [1 undecoded]
  extrude  "Extruded_1098"  [1 undecoded]
  extrude  "Extruded_1099"  [1 undecoded]
  extrude  "Extruded_1100"  [1 undecoded]
  extrude  "Extruded_1101"  [1 undecoded]
  extrude  "Extruded_1102"  [1 undecoded]
  extrude  "Extruded_1103"  [1 undecoded]
  extrude  "Extruded_1104"  [1 undecoded]
  extrude  "Extruded_1105"  [1 undecoded]
  extrude  "Extruded_1106"  [1 undecoded]
  extrude  "Extruded_1107"  [1 undecoded]
  extrude  "Extruded_1108"  [1 undecoded]
  extrude  "Extruded_1109"  [1 undecoded]
  extrude  "Extruded_1110"  [1 undecoded]
  extrude  "Extruded_1111"  [1 undecoded]
  sketch  "3D Sketch1"
  projected_geometry  "Projected Loop1"
  projected_geometry  "Projected Loop2"
  projected_geometry  "Projected Loop3"
  projected_geometry  "Projected Loop4"
  projected_geometry  "Projected Loop5"
  projected_geometry  "Projected Loop6"
  projected_geometry  "Projected Loop7"
  projected_geometry  "Projected Loop8"
  projected_geometry  "Projected Loop9"
  projected_geometry  "Projected Loop10"
  projected_geometry  "Projected Loop11"
  projected_geometry  "Projected Loop12"
  projected_geometry  "Projected Loop13"
  projected_geometry  "Projected Loop14"
  projected_geometry  "Projected Loop15"
  projected_geometry  "Projected Loop16"
  projected_geometry  "Projected Loop17"
  projected_geometry  "Projected Loop18"
  projected_geometry  "Projected Loop19"
  projected_geometry  "Projected Loop20"
  projected_geometry  "Projected Loop21"
  projected_geometry  "Projected Loop22"
  projected_geometry  "Projected Loop23"
  projected_geometry  "Projected Loop24"
  projected_geometry  "Projected Loop25"
  imported_body  "Base1"
  imported_body  "Base2"
  imported_body  "Base3"
  imported_body  "Base4"
  imported_body  "Base5"
  imported_body  "Base6"
  imported_body  "Base7"
  imported_body  "Base8"
  imported_body  "Base9"
  imported_body  "Base10"
  imported_body  "Base11"
  imported_body  "Base12"
  imported_body  "Base13"
  imported_body  "Base14"
  imported_body  "Base15"
  imported_body  "Base16"
  imported_body  "Base17"
  imported_body  "Base18"
  imported_body  "Base19"
  imported_body  "Base20"
  imported_body  "Base21"
  imported_body  "Base22"
  imported_body  "Base23"
  imported_body  "Base24"
  imported_body  "Base25"
  imported_body  "Base26"
  imported_body  "Base27"
  imported_body  "Base28"
  imported_body  "Base29"
  imported_body  "Base30"
  imported_body  "Base31"
  imported_body  "Base32"
  imported_body  "Base33"
  imported_body  "Base34"
  imported_body  "Base35"
  imported_body  "Base36"
  imported_body  "Base37"
  imported_body  "Base38"
  imported_body  "Base39"
  imported_body  "Base40"
  imported_body  "Base41"
  imported_body  "Base42"
  imported_body  "Base43"
  imported_body  "Base44"
  imported_body  "Base45"
  imported_body  "Base46"
  imported_body  "Base47"
  imported_body  "Base48"
  imported_body  "Base49"
  imported_body  "Base50"
  imported_body  "Base51"
  imported_body  "Base52"
  imported_body  "Base53"
  imported_body  "Base54"
  imported_body  "Base55"
  imported_body  "Base56"
  imported_body  "Base57"
  imported_body  "Base58"
  imported_body  "Base59"
  imported_body  "Base60"
  imported_body  "Base61"
  imported_body  "Base62"
  imported_body  "Base63"
  imported_body  "Base64"
  imported_body  "Base65"
  imported_body  "Base66"
  imported_body  "Base67"
  imported_body  "Base68"
  imported_body  "Base69"
  imported_body  "Base70"
  imported_body  "Base71"
  imported_body  "Base72"
  imported_body  "Base73"
  imported_body  "Base74"
  imported_body  "Base75"
  imported_body  "Base76"
  imported_body  "Base77"
  imported_body  "Base78"
  imported_body  "Base79"
  imported_body  "Base80"
  imported_body  "Base81"
  imported_body  "Base82"
  imported_body  "Base83"
  imported_body  "Base84"
  imported_body  "Base85"
  imported_body  "Base86"
  imported_body  "Base87"
  imported_body  "Base88"
  imported_body  "Base89"
  imported_body  "Base90"
  imported_body  "Base91"
  imported_body  "Base92"
  imported_body  "Base93"
  imported_body  "Base94"
  imported_body  "Base95"
  imported_body  "Base96"
  imported_body  "Base97"
  imported_body  "Base98"
  imported_body  "Base99"
  imported_body  "Base100"
  imported_body  "Base101"
  imported_body  "Base102"
  imported_body  "Base103"
  imported_body  "Base104"
  imported_body  "Base105"
  imported_body  "Base106"
  imported_body  "Base107"
  imported_body  "Base108"
  imported_body  "Base109"
  imported_body  "Base110"
  imported_body  "Base111"
  imported_body  "Base112"
  imported_body  "Base113"
  imported_body  "Base114"
  imported_body  "Base115"
  imported_body  "Base116"
  imported_body  "Base117"
  imported_body  "Base118"
  imported_body  "Base119"
  imported_body  "Base120"
  imported_body  "Base121"
  imported_body  "Base122"
  imported_body  "Base123"
  imported_body  "Base124"
  imported_body  "Base125"
  imported_body  "Base126"
  imported_body  "Base127"
  imported_body  "Base128"
  imported_body  "Base129"
  imported_body  "Base130"
  imported_body  "Base131"
  imported_body  "Base132"
  imported_body  "Base133"
  imported_body  "Base134"
  imported_body  "Base135"
  imported_body  "Base136"
  imported_body  "Base137"
  imported_body  "Base138"
  imported_body  "Base139"
  imported_body  "Base140"
  imported_body  "Base141"
  imported_body  "Base142"
  imported_body  "Base143"
  imported_body  "Base144"
  imported_body  "Base145"
  imported_body  "Base146"
  imported_body  "Base147"
  imported_body  "Base148"
  imported_body  "Base149"
  imported_body  "Base150"
  imported_body  "Base151"
  imported_body  "Base152"
  imported_body  "Base153"
  imported_body  "Base154"
  imported_body  "Base155"
  imported_body  "Base156"
  imported_body  "Base157"
  imported_body  "Base158"
  imported_body  "Base159"
  imported_body  "Base160"
  imported_body  "Base161"
  imported_body  "Base162"
  imported_body  "Base163"
  imported_body  "Base164"
  imported_body  "Base165"
  imported_body  "Base166"
  imported_body  "Base167"
  imported_body  "Base168"
  imported_body  "Base169"
  imported_body  "Base170"
  imported_body  "Base171"
  imported_body  "Base172"
  imported_body  "Base173"
  imported_body  "Base174"
  imported_body  "Base175"
  imported_body  "Base176"
  imported_body  "Base177"
  imported_body  "Base178"
  imported_body  "Base179"
  imported_body  "Base180"
  imported_body  "Base181"
  imported_body  "Base182"
  imported_body  "Base183"
  imported_body  "Base184"
  imported_body  "Base185"
  imported_body  "Base186"
  imported_body  "Base187"
  imported_body  "Base188"
  imported_body  "Base189"
  imported_body  "Base190"
  imported_body  "Base191"
  imported_body  "Base192"
  imported_body  "Base193"
  imported_body  "Base194"
  imported_body  "Base195"
  imported_body  "Base196"
  imported_body  "Base197"
  imported_body  "Base198"
  imported_body  "Base199"
  imported_body  "Base200"
  imported_body  "Base201"
  imported_body  "Base202"
  imported_body  "Base203"
  imported_body  "Base204"
  imported_body  "Base205"
  imported_body  "Base206"
  imported_body  "Base207"
  imported_body  "Base208"
  imported_body  "Base209"
  imported_body  "Base210"
  imported_body  "Base211"
  imported_body  "Base212"
  imported_body  "Base213"
  imported_body  "Base214"
  imported_body  "Base215"
  imported_body  "Base216"
  imported_body  "Base217"
  imported_body  "Base218"
  imported_body  "Base219"
  imported_body  "Base220"
  imported_body  "Base221"
  imported_body  "Base222"
  imported_body  "Base223"
  imported_body  "Base224"
  imported_body  "Base225"
  imported_body  "Base226"
  imported_body  "Base227"
  imported_body  "Base228"
  imported_body  "Base229"
  imported_body  "Base230"
  imported_body  "Base231"
  imported_body  "Base232"
  imported_body  "Base233"
  imported_body  "Base234"
  imported_body  "Base235"
  imported_body  "Base236"
  imported_body  "Base237"
  imported_body  "Base238"
  imported_body  "Base239"
  imported_body  "Base240"
  imported_body  "Base241"
  imported_body  "Base242"
  imported_body  "Base243"
  imported_body  "Base244"
  imported_body  "Base245"
  imported_body  "Base246"
  imported_body  "Base247"
  imported_body  "Base248"
  imported_body  "Base249"
  imported_body  "Base250"
  imported_body  "Base251"
  imported_body  "Base252"
  imported_body  "Base253"
  imported_body  "Base254"
  imported_body  "Base255"
  imported_body  "Base256"
  imported_body  "Base257"
  imported_body  "Base258"
  imported_body  "Base259"
  imported_body  "Base260"
  imported_body  "Base261"
  imported_body  "Base262"
  imported_body  "Base263"
  imported_body  "Base264"
  imported_body  "Base265"
  imported_body  "Base266"
  imported_body  "Base267"
  imported_body  "Base268"
  imported_body  "Base269"
  imported_body  "Base270"
  imported_body  "Base271"
  imported_body  "Base272"
  imported_body  "Base273"
  imported_body  "Base274"
  imported_body  "Base275"
  imported_body  "Base276"
  imported_body  "Base277"
  imported_body  "Base278"
  imported_body  "Base279"
  imported_body  "Base280"
  imported_body  "Base281"
  imported_body  "Base282"
  imported_body  "Base283"
  imported_body  "Base284"
  imported_body  "Base285"
  imported_body  "Base286"
  imported_body  "Base287"
  imported_body  "Base288"
  imported_body  "Base289"
  imported_body  "Base290"
  imported_body  "Base291"
  imported_body  "Base292"
  imported_body  "Base293"
  imported_body  "Base294"
  imported_body  "Base295"
  imported_body  "Base296"
  imported_body  "Base297"
  imported_body  "Base298"
  imported_body  "Base299"
  imported_body  "Base300"
  imported_body  "Base301"
  imported_body  "Base302"
  imported_body  "Base303"
  imported_body  "Base304"
  imported_body  "Base305"
  imported_body  "Base306"
  imported_body  "Base307"
  imported_body  "Base308"
  imported_body  "Base309"
  imported_body  "Base310"
  imported_body  "Base311"
  imported_body  "Base312"
  imported_body  "Base313"
  imported_body  "Base314"
  imported_body  "Base315"
  imported_body  "Base316"
  imported_body  "Base317"
  imported_body  "Base318"
  imported_body  "Base319"
  imported_body  "Base320"
  imported_body  "Base321"
  imported_body  "Base322"
  imported_body  "Base323"
  imported_body  "Base324"
  imported_body  "Base325"
  imported_body  "Base326"
  imported_body  "Base327"
  imported_body  "Base328"
  imported_body  "Base329"
  imported_body  "Base330"
  imported_body  "Base331"
  imported_body  "Base332"
  imported_body  "Base333"
  imported_body  "Base334"
  imported_body  "Base335"
  imported_body  "Base336"
  imported_body  "Base337"
  imported_body  "Base338"
  imported_body  "Base339"
  imported_body  "Base340"
  imported_body  "Base341"
  imported_body  "Base342"
  imported_body  "Base343"
  imported_body  "Base344"
  imported_body  "Base345"
  imported_body  "Base346"
  imported_body  "Base347"
  imported_body  "Base348"
  imported_body  "Base349"
  imported_body  "Base350"
  imported_body  "Base351"
  imported_body  "Base352"
  imported_body  "Base353"
  imported_body  "Base354"
  imported_body  "Base355"
  imported_body  "Base356"
  imported_body  "Base357"
  imported_body  "Base358"
  imported_body  "Base359"
  imported_body  "Base360"
  imported_body  "Base361"
  imported_body  "Base362"
  imported_body  "Base363"
  imported_body  "Base364"
  imported_body  "Base365"
  imported_body  "Base366"
  imported_body  "Base367"
  imported_body  "Base368"
  imported_body  "Base369"
  imported_body  "Base370"
  imported_body  "Base371"
  imported_body  "Base372"
  imported_body  "Base373"
  imported_body  "Base374"
  imported_body  "Base375"
  imported_body  "Base376"
  imported_body  "Base377"
  imported_body  "Base378"
  imported_body  "Base379"
  imported_body  "Base380"
  imported_body  "Base381"
  imported_body  "Base382"
  imported_body  "Base383"
  imported_body  "Base384"
  imported_body  "Base385"
  imported_body  "Base386"
  imported_body  "Base387"
  imported_body  "Base388"
  imported_body  "Base389"
  imported_body  "Base390"
  imported_body  "Base391"
  imported_body  "Base392"
  imported_body  "Base393"
  imported_body  "Base394"
  imported_body  "Base395"
  imported_body  "Base396"
  imported_body  "Base397"
  imported_body  "Base398"
  imported_body  "Base399"
  imported_body  "Base400"
  imported_body  "Base401"
  imported_body  "Base402"
  imported_body  "Base403"
  imported_body  "Base404"
  imported_body  "Base405"
  imported_body  "Base406"
  imported_body  "Base407"
  imported_body  "Base408"
  imported_body  "Base409"
  imported_body  "Base410"
  imported_body  "Base411"
  imported_body  "Base412"
  imported_body  "Base413"
  imported_body  "Base414"
  imported_body  "Base415"
  imported_body  "Base416"
  imported_body  "Base417"
  imported_body  "Base418"
  imported_body  "Base419"
  imported_body  "Base420"
  imported_body  "Base421"
  imported_body  "Base422"
  imported_body  "Base423"
  imported_body  "Base424"
  imported_body  "Base425"
  imported_body  "Base426"
  imported_body  "Base427"
  imported_body  "Base428"
  imported_body  "Base429"
  imported_body  "Base430"
  imported_body  "Base431"
  imported_body  "Base432"
  imported_body  "Base433"
  imported_body  "Base434"
  imported_body  "Base435"
  imported_body  "Base436"
  imported_body  "Base437"
  imported_body  "Base438"
  imported_body  "Base439"
  imported_body  "Base440"
  imported_body  "Base441"
  imported_body  "Base442"
  imported_body  "Base443"
  imported_body  "Base444"
  imported_body  "Base445"
  imported_body  "Base446"
  imported_body  "Base447"
  imported_body  "Base448"
  imported_body  "Base449"
  imported_body  "Base450"
  imported_body  "Base451"
  imported_body  "Base452"
  imported_body  "Base453"
  imported_body  "Base454"
  imported_body  "Base455"
  imported_body  "Base456"
  imported_body  "Base457"
  imported_body  "Base458"
  imported_body  "Base459"
  imported_body  "Base460"
  imported_body  "Base461"
  imported_body  "Base462"
  imported_body  "Base463"
  imported_body  "Base464"
  imported_body  "Base465"
  imported_body  "Base466"
  imported_body  "Base467"
  imported_body  "Base468"
  imported_body  "Base469"
  imported_body  "Base470"
  imported_body  "Base471"
  imported_body  "Base472"
  imported_body  "Base473"
  imported_body  "Base474"
  imported_body  "Base475"
  imported_body  "Base476"
  imported_body  "Base477"
  imported_body  "Base478"
  imported_body  "Base479"
  imported_body  "Base480"
  imported_body  "Base481"
  imported_body  "Base482"
  imported_body  "Base483"
  imported_body  "Base484"
  imported_body  "Base485"
  imported_body  "Base486"
  imported_body  "Base487"
  imported_body  "Base488"
  imported_body  "Base489"
  imported_body  "Base490"
  imported_body  "Base491"
  imported_body  "Base492"
  imported_body  "Base493"
  imported_body  "Base494"
  imported_body  "Base495"
  imported_body  "Base496"
  imported_body  "Base497"
  imported_body  "Base498"
  imported_body  "Base499"
  imported_body  "Base500"
  imported_body  "Base501"
  imported_body  "Base502"
  imported_body  "Base503"
  imported_body  "Base504"
  imported_body  "Base505"
  imported_body  "Base506"
  imported_body  "Base507"
  imported_body  "Base508"
  imported_body  "Base509"
  imported_body  "Base510"
  imported_body  "Base511"
  imported_body  "Base512"
  imported_body  "Base513"
  imported_body  "Base514"
  imported_body  "Base515"
  imported_body  "Base516"
  imported_body  "Base517"
  imported_body  "Base518"
  imported_body  "Base519"
  imported_body  "Base520"
  imported_body  "Base521"
  imported_body  "Base522"
  imported_body  "Base523"
  imported_body  "Base524"
  imported_body  "Base525"
  imported_body  "Base526"
  imported_body  "Base527"
  imported_body  "Base528"
  imported_body  "Base529"
  imported_body  "Base530"
  imported_body  "Base531"
  imported_body  "Base532"
  imported_body  "Base533"
  imported_body  "Base534"
  imported_body  "Base535"
  imported_body  "Base536"
  imported_body  "Base537"
  imported_body  "Base538"
  imported_body  "Base539"
  imported_body  "Base540"
  imported_body  "Base541"
  imported_body  "Base542"
  imported_body  "Base543"
  imported_body  "Base544"
  imported_body  "Base545"
  imported_body  "Base546"
  imported_body  "Base547"
  imported_body  "Base548"
  imported_body  "Base549"
  imported_body  "Base550"
  imported_body  "Base551"
  imported_body  "Base552"
  imported_body  "Base553"
  imported_body  "Base554"
  imported_body  "Base555"
  imported_body  "Base556"
  imported_body  "Base557"
  imported_body  "Base558"
  imported_body  "Base559"
  imported_body  "Base560"
  imported_body  "Base561"
  imported_body  "Base562"
  imported_body  "Base563"
  imported_body  "Base564"
  imported_body  "Base565"
  imported_body  "Base566"
  imported_body  "Base567"
  imported_body  "Base568"
  imported_body  "Base569"
  imported_body  "Base570"
  imported_body  "Base571"
  imported_body  "Base572"
  imported_body  "Base573"
  imported_body  "Base574"
  imported_body  "Base575"
  imported_body  "Base576"
  imported_body  "Base577"
  imported_body  "Base578"
  imported_body  "Base579"
  imported_body  "Base580"
  imported_body  "Base581"
  imported_body  "Base582"
  imported_body  "Base583"
  imported_body  "Base584"
  imported_body  "Base585"
  imported_body  "Base586"
  imported_body  "Base587"
  imported_body  "Base588"
  imported_body  "Base589"
  imported_body  "Base590"
  imported_body  "Base591"
  imported_body  "Base592"
  imported_body  "Base593"
  imported_body  "Base594"
  imported_body  "Base595"
  imported_body  "Base596"
  imported_body  "Base597"
  imported_body  "Base598"
  imported_body  "Base599"
  imported_body  "Base600"
  imported_body  "Base601"
  imported_body  "Base602"
  imported_body  "Base603"
  imported_body  "Base604"
  imported_body  "Base605"
  imported_body  "Base606"
  imported_body  "Base607"
  imported_body  "Base608"
  imported_body  "Base609"
  imported_body  "Base610"
  imported_body  "Base611"
  imported_body  "Base612"
  imported_body  "Base613"
  imported_body  "Base614"
  imported_body  "Base615"
  imported_body  "Base616"
  imported_body  "Base617"
  imported_body  "Base618"
  imported_body  "Base619"
  imported_body  "Base620"
  imported_body  "Base621"
  imported_body  "Base622"
  imported_body  "Base623"
  imported_body  "Base624"
  imported_body  "Base625"
  imported_body  "Base626"
  imported_body  "Base627"
  imported_body  "Base628"
  imported_body  "Base629"
  imported_body  "Base630"
  imported_body  "Base631"
  imported_body  "Base632"
  imported_body  "Base633"
  imported_body  "Base634"
  imported_body  "Base635"
  imported_body  "Base636"
  imported_body  "Base637"
  imported_body  "Base638"
  imported_body  "Base639"
  imported_body  "Base640"
  imported_body  "Base641"
  imported_body  "Base642"
  imported_body  "Base643"
  imported_body  "Base644"
  imported_body  "Base645"
  imported_body  "Base646"
  imported_body  "Base647"
  imported_body  "Base648"
  imported_body  "Base649"
  imported_body  "Base650"
  imported_body  "Base651"
  imported_body  "Base652"
  imported_body  "Base653"
  imported_body  "Base654"
  imported_body  "Base655"
  imported_body  "Base656"
  imported_body  "Base657"
  imported_body  "Base658"
  imported_body  "Base659"
  imported_body  "Base660"
  imported_body  "Base661"
  imported_body  "Base662"
  imported_body  "Base663"
  imported_body  "Base664"
  imported_body  "Base665"
  imported_body  "Base666"
  imported_body  "Base667"
  imported_body  "Base668"
  imported_body  "Base669"
  imported_body  "Base670"
  imported_body  "Base671"
  imported_body  "Base672"
  imported_body  "Base673"
  imported_body  "Base674"
  imported_body  "Base675"
  imported_body  "Base676"
  imported_body  "Base677"
  imported_body  "Base678"
  imported_body  "Base679"
  imported_body  "Base680"
  imported_body  "Base681"
  imported_body  "Base682"
  imported_body  "Base683"
  imported_body  "Base684"
  imported_body  "Base685"
  imported_body  "Base686"
  imported_body  "Base687"
  imported_body  "Base688"
  imported_body  "Base689"
  imported_body  "Base690"
  imported_body  "Base691"
  imported_body  "Base692"
  imported_body  "Base693"
  imported_body  "Base694"
  imported_body  "Base695"
  imported_body  "Base696"
  imported_body  "Base697"
  imported_body  "Base698"
  imported_body  "Base699"
  imported_body  "Base700"
  imported_body  "Base701"
  imported_body  "Base702"
  imported_body  "Base703"
  imported_body  "Base704"
  imported_body  "Base705"
  imported_body  "Base706"
  imported_body  "Base707"
  imported_body  "Base708"
  imported_body  "Base709"
  imported_body  "Base710"
  imported_body  "Base711"
  imported_body  "Base712"
  imported_body  "Base713"
  imported_body  "Base714"
  imported_body  "Base715"
  imported_body  "Base716"
  imported_body  "Base717"
  imported_body  "Base718"
  imported_body  "Base719"
  imported_body  "Base720"
  imported_body  "Base721"
  imported_body  "Base722"
  imported_body  "Base723"
  imported_body  "Base724"
  imported_body  "Base725"
  imported_body  "Base726"
  imported_body  "Base727"
  imported_body  "Base728"
  imported_body  "Base729"
  imported_body  "Base730"
  imported_body  "Base731"
  imported_body  "Base732"
  imported_body  "Base733"
  imported_body  "Base734"
  imported_body  "Base735"
  imported_body  "Base736"
  imported_body  "Base737"
  imported_body  "Base738"
  imported_body  "Base739"
  imported_body  "Base740"
  imported_body  "Base741"
  imported_body  "Base742"
  imported_body  "Base743"
  imported_body  "Base744"
  imported_body  "Base745"
  imported_body  "Base746"
  imported_body  "Base747"
  imported_body  "Base748"
  imported_body  "Base749"
  imported_body  "Base750"
  imported_body  "Base751"
  imported_body  "Base752"
  imported_body  "Base753"
  imported_body  "Base754"
  imported_body  "Base755"
  imported_body  "Base756"
  imported_body  "Base757"
  imported_body  "Base758"
  imported_body  "Base759"
  imported_body  "Base760"
  imported_body  "Base761"
  imported_body  "Base762"
  imported_body  "Base763"
  imported_body  "Base764"
  imported_body  "Base765"
  imported_body  "Base766"
  imported_body  "Base767"
  imported_body  "Base768"
  imported_body  "Base769"
  imported_body  "Base770"
  imported_body  "Base771"
  imported_body  "Base772"
  imported_body  "Base773"
  imported_body  "Base774"
  imported_body  "Base775"
  imported_body  "Base776"
  imported_body  "Base777"
  imported_body  "Base778"
  imported_body  "Base779"
  imported_body  "Base780"
  imported_body  "Base781"
  imported_body  "Base782"
  imported_body  "Base783"
  imported_body  "Base784"
  imported_body  "Base785"
  imported_body  "Base786"
  imported_body  "Base787"
  imported_body  "Base788"
  imported_body  "Base789"
  imported_body  "Base790"
  imported_body  "Base791"
  imported_body  "Base792"
  imported_body  "Base793"
  imported_body  "Base794"
  imported_body  "Base795"
  imported_body  "Base796"
  imported_body  "Base797"
  imported_body  "Base798"
  imported_body  "Base799"
  imported_body  "Base800"
  imported_body  "Base801"
  imported_body  "Base802"
  imported_body  "Base803"
  imported_body  "Base804"
  imported_body  "Base805"
  imported_body  "Base806"
  imported_body  "Base807"
  imported_body  "Base808"
  imported_body  "Base809"
  imported_body  "Base810"
  imported_body  "Base811"
  imported_body  "Base812"
  imported_body  "Base813"
  imported_body  "Base814"
  imported_body  "Base815"
  imported_body  "Base816"
  imported_body  "Base817"
  imported_body  "Base818"
  imported_body  "Base819"
  imported_body  "Base820"
  imported_body  "Base821"
  imported_body  "Base822"
  imported_body  "Base823"
  imported_body  "Base824"
  imported_body  "Base825"
  imported_body  "Base826"
  imported_body  "Base827"
  imported_body  "Base828"
  imported_body  "Base829"
  imported_body  "Base830"
  imported_body  "Base831"
  imported_body  "Base832"
  imported_body  "Base833"
  imported_body  "Base834"
  imported_body  "Base835"
  imported_body  "Base836"
  imported_body  "Base837"
  imported_body  "Base838"
  imported_body  "Base839"
  imported_body  "Base840"
  imported_body  "Base841"
  imported_body  "Base842"
  imported_body  "Base843"
  imported_body  "Base844"
  imported_body  "Base845"
  imported_body  "Base846"
  imported_body  "Base847"
  imported_body  "Base848"
  imported_body  "Base849"
  imported_body  "Base850"
  imported_body  "Base851"
  imported_body  "Base852"
  imported_body  "Base853"
  imported_body  "Base854"
  imported_body  "Base855"
  imported_body  "Base856"
  imported_body  "Base857"
  imported_body  "Base858"
  imported_body  "Base859"
  imported_body  "Base860"
  imported_body  "Base861"
  imported_body  "Base862"
  imported_body  "Base863"
  imported_body  "Base864"
  imported_body  "Base865"
  imported_body  "Base866"
  imported_body  "Base867"
  imported_body  "Base868"
  imported_body  "Base869"
  imported_body  "Base870"
  imported_body  "Base871"
  imported_body  "Base872"
  imported_body  "Base873"
  imported_body  "Base874"
  imported_body  "Base875"
  imported_body  "Base876"
  imported_body  "Base877"
  imported_body  "Base878"
  imported_body  "Base879"
  imported_body  "Base880"
  imported_body  "Base881"
  imported_body  "Base882"
  imported_body  "Base883"
  imported_body  "Base884"
  imported_body  "Base885"
  imported_body  "Base886"
  imported_body  "Base887"
  imported_body  "Base888"
  imported_body  "Base889"
  imported_body  "Base890"
  imported_body  "Base891"
  imported_body  "Base892"
  imported_body  "Base893"
  imported_body  "Base894"
  imported_body  "Base895"
  imported_body  "Base896"
  imported_body  "Base897"
  imported_body  "Base898"
  imported_body  "Base899"
  imported_body  "Base900"
  imported_body  "Base901"
  imported_body  "Base902"
  imported_body  "Base903"
  imported_body  "Base904"
  imported_body  "Base905"
  imported_body  "Base906"
  imported_body  "Base907"
  imported_body  "Base908"
  imported_body  "Base909"
  imported_body  "Base910"
  imported_body  "Base911"
  imported_body  "Base912"
  imported_body  "Base913"
  imported_body  "Base914"
  imported_body  "Base915"
  imported_body  "Base916"
  imported_body  "Base917"
  imported_body  "Base918"
  imported_body  "Base919"
  imported_body  "Base920"
  imported_body  "Base921"
  imported_body  "Base922"
  imported_body  "Base923"
  imported_body  "Base924"
  imported_body  "Base925"
  imported_body  "Base926"
  imported_body  "Base927"
  imported_body  "Base928"
  imported_body  "Base929"
  imported_body  "Base930"
  imported_body  "Base931"
  imported_body  "Base932"
  imported_body  "Base933"
  imported_body  "Base934"
  imported_body  "Base935"
  imported_body  "Base936"
  imported_body  "Base937"
  imported_body  "Base938"
  imported_body  "Base939"
  imported_body  "Base940"
  imported_body  "Base941"
  imported_body  "Base942"
  imported_body  "Base943"
  imported_body  "Base944"
  imported_body  "Base945"
  imported_body  "Base946"
  imported_body  "Base947"
  imported_body  "Base948"
  imported_body  "Base949"
  imported_body  "Base950"
  imported_body  "Base951"
  imported_body  "Base952"
  imported_body  "Base953"
  imported_body  "Base954"
  imported_body  "Base955"
  imported_body  "Base956"
  imported_body  "Base957"
  imported_body  "Base958"
  imported_body  "Base959"
  imported_body  "Base960"
  imported_body  "Base961"
  imported_body  "Base962"
  imported_body  "Base963"
  imported_body  "Base964"
  imported_body  "Base965"
  imported_body  "Base966"
  imported_body  "Base967"
  imported_body  "Base968"
  imported_body  "Base969"
  imported_body  "Base970"
  imported_body  "Base971"
  imported_body  "Base972"
  imported_body  "Base973"
  imported_body  "Base974"
  imported_body  "Base975"
  imported_body  "Base976"
  imported_body  "Base977"
  imported_body  "Base978"
  imported_body  "Base979"
  imported_body  "Base980"
  imported_body  "Base981"
  imported_body  "Base982"
  imported_body  "Base983"
  imported_body  "Base984"
  imported_body  "Base985"
  imported_body  "Base986"
  imported_body  "Base987"
  imported_body  "Base988"
  imported_body  "Base989"
  imported_body  "Base990"
  imported_body  "Base991"
  imported_body  "Base992"
  imported_body  "Base993"
  imported_body  "Base994"
  imported_body  "Base995"
  imported_body  "Base996"
  imported_body  "Base997"
  imported_body  "Base998"
  imported_body  "Base999"
  imported_body  "Base1000"
  imported_body  "Base1001"
  imported_body  "Base1002"
  imported_body  "Base1003"
  imported_body  "Base1004"
  imported_body  "Base1005"
  imported_body  "Base1006"
  imported_body  "Base1007"
  imported_body  "Base1008"
  imported_body  "Base1009"
  imported_body  "Base1010"
  imported_body  "Base1011"
  imported_body  "Base1012"
  imported_body  "Base1013"
  imported_body  "Base1014"
  imported_body  "Base1015"
  imported_body  "Base1016"
  imported_body  "Base1017"
  imported_body  "Base1018"
  imported_body  "Base1019"
  imported_body  "Base1020"
  imported_body  "Base1021"
  imported_body  "Base1022"
  imported_body  "Base1023"
  imported_body  "Base1024"
  imported_body  "Base1025"
  imported_body  "Base1026"
  imported_body  "Base1027"
  imported_body  "Base1028"
  imported_body  "Base1029"
  imported_body  "Base1030"
  imported_body  "Base1031"
  imported_body  "Base1032"
  imported_body  "Base1033"
  imported_body  "Base1034"
  imported_body  "Base1035"
  imported_body  "Base1036"
  imported_body  "Base1037"
  imported_body  "Base1038"
  imported_body  "Base1039"
  imported_body  "Base1040"
  imported_body  "Base1041"
  imported_body  "Base1042"
  imported_body  "Base1043"
  imported_body  "Base1044"
  imported_body  "Base1045"
  imported_body  "Base1046"
  imported_body  "Base1047"
  imported_body  "Base1048"
  imported_body  "Base1049"
  imported_body  "Base1050"
  imported_body  "Base1051"
  imported_body  "Base1052"
  imported_body  "Base1053"
  imported_body  "Base1054"
  imported_body  "Base1055"
  imported_body  "Base1056"
  imported_body  "Base1057"
  imported_body  "Base1058"
  imported_body  "Base1059"
  imported_body  "Base1060"
  imported_body  "Base1061"
  imported_body  "Base1062"
  imported_body  "Base1063"
  imported_body  "Base1064"
  imported_body  "Base1065"
  imported_body  "Base1066"
  imported_body  "Base1067"
  imported_body  "Base1068"
  imported_body  "Base1069"
  imported_body  "Base1070"
  imported_body  "Base1071"
  imported_body  "Base1072"
  imported_body  "Base1073"
  imported_body  "Base1074"
  imported_body  "Base1075"
  imported_body  "Base1076"
  imported_body  "Base1077"
  imported_body  "Base1078"
  imported_body  "Base1079"
  imported_body  "Base1080"
  imported_body  "Base1081"
  imported_body  "Base1082"
  imported_body  "Base1083"
  imported_body  "Base1084"
  imported_body  "Base1085"
  imported_body  "Base1086"
  imported_body  "Base1087"
  imported_body  "Base1088"
  imported_body  "Base1089"
  imported_body  "Base1090"
  imported_body  "Base1091"
  imported_body  "Base1092"
  imported_body  "Base1093"
  imported_body  "Base1094"
  imported_body  "Base1095"
  imported_body  "Base1096"
  imported_body  "Base1097"
  imported_body  "Base1098"
  imported_body  "Base1099"
  imported_body  "Base1100"
  imported_body  "Base1101"
  imported_body  "Base1102"
  imported_body  "Base1103"
  imported_body  "Base1104"
  imported_body  "Base1105"
  imported_body  "Base1106"
  imported_body  "Base1107"
  imported_body  "Base1108"
  imported_body  "Base1109"
  imported_body  "Base1110"
  imported_body  "Base1111"
  imported_body  "Base1112"
  imported_body  "Base1113"
  imported_body  "Base1114"
  imported_body  "Base1115"
  imported_body  "Base1116"
  imported_body  "Base1117"
  imported_body  "Base1118"
  imported_body  "Base1119"
  imported_body  "Base1120"
  imported_body  "Base1121"
  imported_body  "Base1122"
  imported_body  "Base1123"
  imported_body  "Base1124"
  imported_body  "Base1125"
  imported_body  "Base1126"
  imported_body  "Base1127"
  imported_body  "Base1128"
  imported_body  "Base1129"
  imported_body  "Base1130"
  imported_body  "Base1131"
  imported_body  "Base1132"
  imported_body  "Base1133"
  imported_body  "Base1134"
  imported_body  "Base1135"
  imported_body  "Base1136"
  imported_body  "Base1137"
  imported_body  "Base1138"
  imported_body  "Base1139"
  imported_body  "Base1140"
  imported_body  "Base1141"
  imported_body  "Base1142"
  imported_body  "Base1143"
  imported_body  "Base1144"
  imported_body  "Base1145"
  imported_body  "Base1146"
  imported_body  "Base1147"
  imported_body  "Base1148"
  imported_body  "Base1149"
  imported_body  "Base1150"
  imported_body  "Base1151"
  imported_body  "Base1152"
  imported_body  "Base1153"
  imported_body  "Base1154"
  imported_body  "Base1155"
  imported_body  "Base1156"
  imported_body  "Base1157"
  imported_body  "Base1158"
  imported_body  "Base1159"
  imported_body  "Base1160"
  imported_body  "Base1161"
  imported_body  "Base1162"
  imported_body  "Base1163"
note: 1098 required parameter values undecoded (feature->parameter linkage not recoverable at this tier; creation-order binding heuristic only, values carry confidence <= 0.55)
